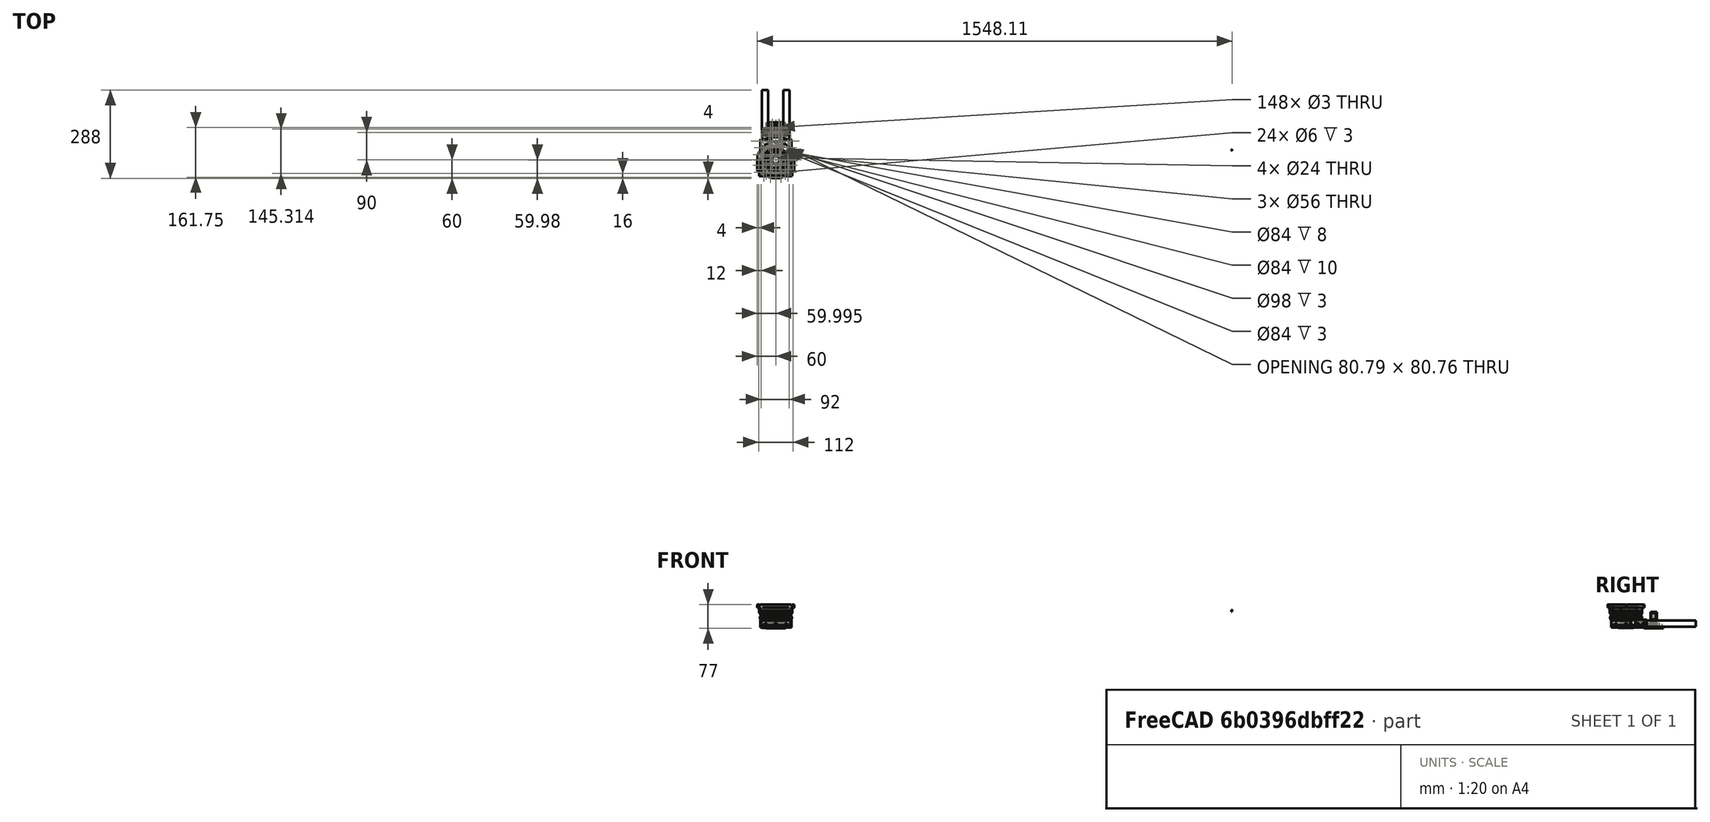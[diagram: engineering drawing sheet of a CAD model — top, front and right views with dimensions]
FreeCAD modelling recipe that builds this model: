
FCSTD DOCUMENT  (FreeCAD 0.19R24276 (Git))
Label: J-max_encoder_026
License: All rights reserved
LicenseURL: http://en.wikipedia.org/wiki/All_rights_reserved
objects: Part::Cylinder×255, Part::Compound×99, Part::Cut×96, Part::Box×95, Part::Chamfer×22, Part::FeaturePython×21, Part::MultiFuse×6, Part::Fillet×5, Mesh::Feature×5, Part::Mirroring×2
note: 601 computed .brp shape members not serialized (recipe doc carries the construction recipe); baked Part::Feature solids carry a one-line shape summary decoded from their .brp

FEATURE [Part::Cylinder] Cylinder120  label="Válec120"
  Angle = 360
  AttacherType = Attacher::AttachEngine3D
  Height = 10
  Radius = 52
FEATURE [Part::Cylinder] Cylinder121  label="Válec121"
  Angle = 360
  AttacherType = Attacher::AttachEngine3D
  Height = 10
  Radius = 60
FEATURE [Part::FeaturePython] wormgear026  # WARN: FeaturePython — macro-defined, semantics opaque (R4)
  AttacherType = Attacher::AttachEngine3D
  beta = 29.7292
  clearance = 0.25
  diameter = 78.8
  head = 0
  height = 20
  module = 1
  pressure_angle = 20
  reverse_pitch = true
  teeth = 45
  version = 0.0.3
FEATURE [Part::Cut] Cut057
  Base = -> Cylinder121
  Placement = pos=(0,0,10) rot=(0,0,1;0.034907rad)
  Tool = -> wormgear026
FEATURE [Part::FeaturePython] wormgear027  # WARN: FeaturePython — macro-defined, semantics opaque (R4)
  AttacherType = Attacher::AttachEngine3D
  Placement = pos=(0,0,0) rot=(0,0,1;0.009355rad)
  beta = 29.7292
  clearance = 0.25
  diameter = 78.8
  head = 0
  height = 20
  module = 1
  pressure_angle = 20
  reverse_pitch = false
  teeth = 45
  version = 0.0.3
FEATURE [Part::Cut] Cut056
  Base = -> Cylinder120
  Tool = -> wormgear027
FEATURE [Part::Compound] Compound157
  Links = -> [Cut057,Cut056]
FEATURE [Part::Cylinder] Cylinder132  label="Válec132"
  Angle = 360
  AttacherType = Attacher::AttachEngine3D
  Height = 40
  Placement = pos=(59,-17,0) rot=(0,0,1;0rad)
  Radius = 10
FEATURE [Part::Cylinder] Cylinder133  label="Válec133"
  Angle = 360
  AttacherType = Attacher::AttachEngine3D
  Height = 40
  Placement = pos=(-59,-17,0) rot=(0,0,1;0rad)
  Radius = 10
FEATURE [Part::Compound] Compound162
  Links = -> [Cylinder132,Cylinder133]
FEATURE [Part::Cylinder] Cylinder134  label="Válec134"
  Angle = 360
  AttacherType = Attacher::AttachEngine3D
  Height = 10
  Placement = pos=(0,0,20) rot=(0,0,1;0rad)
  Radius = 52
FEATURE [Part::Box] Box045  label="Krychle045"
  AttacherType = Attacher::AttachEngine3D
  Height = 10
  Length = 108
  Placement = pos=(-54,-53,20) rot=(0,0,1;0rad)
  Width = 36
FEATURE [Part::Cut] Cut062
  Base = -> Box045
  Placement = pos=(0,0,-20) rot=(0,0,1;0rad)
  Tool = -> Cylinder134
FEATURE [Part::Cut] Cut063
  Base = -> Cut062
  Tool = -> Compound162
FEATURE [Part::Cylinder] Cylinder135  label="Válec135"
  Angle = 360
  AttacherType = Attacher::AttachEngine3D
  Height = 10
  Placement = pos=(0,0,20) rot=(0,0,1;0rad)
  Radius = 52
FEATURE [Part::Box] Box046  label="Krychle046"
  AttacherType = Attacher::AttachEngine3D
  Height = 10
  Length = 108
  Placement = pos=(-54,-53,20) rot=(0,0,1;0rad)
  Width = 36
FEATURE [Part::Cut] Cut064
  Base = -> Box046
  Placement = pos=(0,0,-10) rot=(0,0,1;0rad)
  Tool = -> Cylinder135
FEATURE [Part::Cylinder] Cylinder136  label="Válec136"
  Angle = 360
  AttacherType = Attacher::AttachEngine3D
  Height = 20
  Placement = pos=(-24,-40,-5) rot=(1,0,0;1.5708rad)
  Radius = 1.5
FEATURE [Part::Cylinder] Cylinder137  label="Válec137"
  Angle = 360
  AttacherType = Attacher::AttachEngine3D
  Height = 20
  Placement = pos=(24,-40,-5) rot=(1,0,0;1.5708rad)
  Radius = 1.5
FEATURE [Part::Box] Box047  label="Krychle047"
  AttacherType = Attacher::AttachEngine3D
  Height = 6
  Length = 6
  Placement = pos=(-27,-47,-8) rot=(0,0,1;0rad)
  Width = 2
FEATURE [Part::Box] Box048  label="Krychle048"
  AttacherType = Attacher::AttachEngine3D
  Height = 6
  Length = 6
  Placement = pos=(21,-47,-8) rot=(0,0,1;0rad)
  Width = 2
FEATURE [Part::FeaturePython] Tube  # WARN: FeaturePython — macro-defined, semantics opaque (R4)
  AttacherType = Attacher::AttachEngine3D
  Height = 8
  InnerRadius = 42
  OuterRadius = 52
  Placement = pos=(0,0,-8) rot=(0,0,1;0rad)
FEATURE [Part::Box] Box049  label="Krychle049"
  AttacherType = Attacher::AttachEngine3D
  Height = 6
  Length = 6
  Placement = pos=(48,-45,4) rot=(0,0,1;0rad)
  Width = 2
FEATURE [Part::Cylinder] Cylinder138  label="Válec138"
  Angle = 360
  AttacherType = Attacher::AttachEngine3D
  Height = 40
  Placement = pos=(59,-17,0) rot=(0,0,1;0rad)
  Radius = 10
FEATURE [Part::Cylinder] Cylinder139  label="Válec139"
  Angle = 360
  AttacherType = Attacher::AttachEngine3D
  Height = 40
  Placement = pos=(-59,-17,0) rot=(0,0,1;0rad)
  Radius = 10
FEATURE [Part::Cylinder] Cylinder140  label="Válec140"
  Angle = 360
  AttacherType = Attacher::AttachEngine3D
  Height = 8
  Placement = pos=(0,0,20) rot=(0,0,1;0rad)
  Radius = 52
FEATURE [Part::Compound] Compound163
  Links = -> [Cylinder138,Cylinder139]
FEATURE [Part::Box] Box050  label="Krychle050"
  AttacherType = Attacher::AttachEngine3D
  Height = 8
  Length = 108
  Placement = pos=(-54,-53,20) rot=(0,0,1;0rad)
  Width = 36
FEATURE [Part::Cut] Cut065
  Base = -> Box050
  Placement = pos=(0,0,-20) rot=(0,0,1;0rad)
  Tool = -> Cylinder140
FEATURE [Part::Cut] Cut066
  Base = -> Cut065
  Placement = pos=(0,0,-8) rot=(0,0,1;0rad)
  Tool = -> Compound163
FEATURE [Part::Cylinder] Cylinder141  label="Válec141"
  Angle = 360
  AttacherType = Attacher::AttachEngine3D
  Height = 20
  Placement = pos=(51,-40,7) rot=(1,0,0;1.5708rad)
  Radius = 1.5
FEATURE [Part::Box] Box051  label="Krychle051"
  AttacherType = Attacher::AttachEngine3D
  Height = 6
  Length = 6
  Placement = pos=(-54,-45,4) rot=(0,0,1;0rad)
  Width = 2
FEATURE [Part::Compound] Compound169
  Links = -> [Box047,Box048,Box049,Box051]
FEATURE [Part::Cylinder] Cylinder142  label="Válec142"
  Angle = 360
  AttacherType = Attacher::AttachEngine3D
  Height = 20
  Placement = pos=(-51,-40,7) rot=(1,0,0;1.5708rad)
  Radius = 1.5
FEATURE [Part::Compound] Compound172
  Links = -> [Cylinder136,Cylinder137,Cylinder141,Cylinder142]
FEATURE [Part::Cylinder] Cylinder143  label="Válec143"
  Angle = 360
  AttacherType = Attacher::AttachEngine3D
  Height = 20
  Placement = pos=(0,-56,2) rot=(0,0,1;0rad)
  Radius = 1.5
FEATURE [Part::Cylinder] Cylinder144  label="Válec144"
  Angle = 360
  AttacherType = Attacher::AttachEngine3D
  Height = 20
  Placement = pos=(39.598,-39.598,2) rot=(0,0,1;0.785398rad)
  Radius = 1.5
FEATURE [Part::Cylinder] Cylinder145  label="Válec145"
  Angle = 360
  AttacherType = Attacher::AttachEngine3D
  Height = 20
  Placement = pos=(56,0,2) rot=(0,0,1;1.5708rad)
  Radius = 1.5
FEATURE [Part::Cylinder] Cylinder146  label="Válec146"
  Angle = 360
  AttacherType = Attacher::AttachEngine3D
  Height = 20
  Placement = pos=(39.598,39.598,2) rot=(0,0,1;2.35619rad)
  Radius = 1.5
FEATURE [Part::Cylinder] Cylinder147  label="Válec147"
  Angle = 360
  AttacherType = Attacher::AttachEngine3D
  Height = 20
  Placement = pos=(-1.2e-14,56,2) rot=(0,0,1;3.14159rad)
  Radius = 1.5
FEATURE [Part::Cylinder] Cylinder148  label="Válec148"
  Angle = 360
  AttacherType = Attacher::AttachEngine3D
  Height = 20
  Placement = pos=(-39.598,39.598,2) rot=(0,0,1;3.92699rad)
  Radius = 1.5
FEATURE [Part::Cylinder] Cylinder149  label="Válec149"
  Angle = 360
  AttacherType = Attacher::AttachEngine3D
  Height = 20
  Placement = pos=(-56,-1.3e-14,2) rot=(0,0,-1;1.5708rad)
  Radius = 1.5
FEATURE [Part::Cylinder] Cylinder150  label="Válec150"
  Angle = 360
  AttacherType = Attacher::AttachEngine3D
  Height = 20
  Placement = pos=(-39.598,-39.598,2) rot=(0,0,-1;0.785398rad)
  Radius = 1.5
FEATURE [Part::Compound] Compound164
  Links = -> [Cylinder143,Cylinder144,Cylinder145,Cylinder146,Cylinder147,Cylinder148,Cylinder149,Cylinder150]
FEATURE [Part::Cut] Cut067
  Base = -> Compound157
  Tool = -> Compound164
FEATURE [Part::Cylinder] Cylinder151  label="Válec151"
  Angle = 360
  AttacherType = Attacher::AttachEngine3D
  Height = 20
  Placement = pos=(-39.598,39.598,2) rot=(0,0,1;3.92699rad)
  Radius = 1.5
FEATURE [Part::Cylinder] Cylinder152  label="Válec152"
  Angle = 360
  AttacherType = Attacher::AttachEngine3D
  Height = 20
  Placement = pos=(-39.598,-39.598,2) rot=(0,0,-1;0.785398rad)
  Radius = 1.5
FEATURE [Part::Cylinder] Cylinder153  label="Válec153"
  Angle = 360
  AttacherType = Attacher::AttachEngine3D
  Height = 20
  Placement = pos=(56,0,2) rot=(0,0,1;1.5708rad)
  Radius = 1.5
FEATURE [Part::Cylinder] Cylinder154  label="Válec154"
  Angle = 360
  AttacherType = Attacher::AttachEngine3D
  Height = 20
  Placement = pos=(-1.2e-14,56,2) rot=(0,0,1;3.14159rad)
  Radius = 1.5
FEATURE [Part::Cylinder] Cylinder155  label="Válec155"
  Angle = 360
  AttacherType = Attacher::AttachEngine3D
  Height = 20
  Placement = pos=(0,-56,2) rot=(0,0,1;0rad)
  Radius = 1.5
FEATURE [Part::Cylinder] Cylinder156  label="Válec156"
  Angle = 360
  AttacherType = Attacher::AttachEngine3D
  Height = 20
  Placement = pos=(39.598,39.598,2) rot=(0,0,1;2.35619rad)
  Radius = 1.5
FEATURE [Part::Cylinder] Cylinder157  label="Válec157"
  Angle = 360
  AttacherType = Attacher::AttachEngine3D
  Height = 20
  Placement = pos=(-56,-1.3e-14,2) rot=(0,0,-1;1.5708rad)
  Radius = 1.5
FEATURE [Part::Cylinder] Cylinder158  label="Válec158"
  Angle = 360
  AttacherType = Attacher::AttachEngine3D
  Height = 20
  Placement = pos=(39.598,-39.598,2) rot=(0,0,1;0.785398rad)
  Radius = 1.5
FEATURE [Part::Compound] Compound165
  Links = -> [Cylinder155,Cylinder158,Cylinder153,Cylinder156,Cylinder154,Cylinder151,Cylinder157,Cylinder152]
FEATURE [Part::Cut] Cut068
  Base = -> Cut064
  Tool = -> Compound165
FEATURE [Part::Cylinder] Cylinder159  label="Válec159"
  Angle = 360
  AttacherType = Attacher::AttachEngine3D
  Height = 20
  Placement = pos=(-39.6,-39.6,-10) rot=(0,0,-1;0.785398rad)
  Radius = 4
FEATURE [Part::Cylinder] Cylinder160  label="Válec160"
  Angle = 360
  AttacherType = Attacher::AttachEngine3D
  Height = 20
  Placement = pos=(39.6,-39.6,-10) rot=(0,0,1;0.785398rad)
  Radius = 4
FEATURE [Part::Compound] Compound166
  Links = -> [Cylinder159,Cylinder160]
FEATURE [Part::Cylinder] Cylinder161  label="Válec161"
  Angle = 360
  AttacherType = Attacher::AttachEngine3D
  Height = 20
  Placement = pos=(39.6,-39.6,-10) rot=(0,0,1;0.785398rad)
  Radius = 4
FEATURE [Part::Cylinder] Cylinder162  label="Válec162"
  Angle = 360
  AttacherType = Attacher::AttachEngine3D
  Height = 20
  Placement = pos=(-39.6,-39.6,-10) rot=(0,0,-1;0.785398rad)
  Radius = 4
FEATURE [Part::Compound] Compound167
  Links = -> [Cylinder162,Cylinder161]
FEATURE [Part::Cut] Cut069
  Base = -> Cut067
  Tool = -> Compound166
FEATURE [Part::Cut] Cut070
  Base = -> Cut066
  Tool = -> Compound167
FEATURE [Part::Cut] Cut072
  Base = -> Cut070
  Tool = -> Compound169
FEATURE [Part::Cylinder] Cylinder163  label="Válec163"
  Angle = 360
  AttacherType = Attacher::AttachEngine3D
  Height = 20
  Placement = pos=(39.6,-39.6,-10) rot=(0,0,1;0.785398rad)
  Radius = 4
FEATURE [Part::Cylinder] Cylinder164  label="Válec164"
  Angle = 360
  AttacherType = Attacher::AttachEngine3D
  Height = 20
  Placement = pos=(-39.6,-39.6,-10) rot=(0,0,-1;0.785398rad)
  Radius = 4
FEATURE [Part::Compound] Compound168
  Links = -> [Cylinder164,Cylinder163]
FEATURE [Part::Cut] Cut071
  Base = -> Cut063
  Tool = -> Compound168
FEATURE [Part::Box] Box052  label="Krychle052"
  AttacherType = Attacher::AttachEngine3D
  Height = 6
  Length = 6
  Placement = pos=(48,-45,4) rot=(0,0,1;0rad)
  Width = 2
FEATURE [Part::Box] Box053  label="Krychle053"
  AttacherType = Attacher::AttachEngine3D
  Height = 6
  Length = 6
  Placement = pos=(17,-47,-8) rot=(0,0,1;0rad)
  Width = 2
FEATURE [Part::Box] Box054  label="Krychle054"
  AttacherType = Attacher::AttachEngine3D
  Height = 6
  Length = 6
  Placement = pos=(-23,-47,-8) rot=(0,0,1;0rad)
  Width = 2
FEATURE [Part::Box] Box055  label="Krychle055"
  AttacherType = Attacher::AttachEngine3D
  Height = 6
  Length = 6
  Placement = pos=(-54,-45,4) rot=(0,0,1;0rad)
  Width = 2
FEATURE [Part::Compound] Compound170
  Links = -> [Box054,Box053,Box052,Box055]
FEATURE [Part::Cut] Cut073
  Base = -> Cut071
  Tool = -> Compound170
FEATURE [Part::Box] Box056  label="Krychle056"
  AttacherType = Attacher::AttachEngine3D
  Height = 6
  Length = 6
  Placement = pos=(48,-45,4) rot=(0,0,1;0rad)
  Width = 2
FEATURE [Part::Box] Box057  label="Krychle057"
  AttacherType = Attacher::AttachEngine3D
  Height = 6
  Length = 6
  Placement = pos=(21,-47,-8) rot=(0,0,1;0rad)
  Width = 2
FEATURE [Part::Box] Box058  label="Krychle058"
  AttacherType = Attacher::AttachEngine3D
  Height = 6
  Length = 6
  Placement = pos=(-27,-47,-8) rot=(0,0,1;0rad)
  Width = 2
FEATURE [Part::Box] Box059  label="Krychle059"
  AttacherType = Attacher::AttachEngine3D
  Height = 6
  Length = 6
  Placement = pos=(-54,-45,4) rot=(0,0,1;0rad)
  Width = 2
FEATURE [Part::Compound] Compound171
  Links = -> [Box058,Box057,Box056,Box059]
FEATURE [Part::Cylinder] Cylinder165  label="Válec165"
  Angle = 360
  AttacherType = Attacher::AttachEngine3D
  Height = 20
  Placement = pos=(-24,-40,-5) rot=(1,0,0;1.5708rad)
  Radius = 1.5
FEATURE [Part::Cylinder] Cylinder166  label="Válec166"
  Angle = 360
  AttacherType = Attacher::AttachEngine3D
  Height = 20
  Placement = pos=(24,-40,-5) rot=(1,0,0;1.5708rad)
  Radius = 1.5
FEATURE [Part::Cut] Cut074
  Base = -> Tube
  Tool = -> Compound171
FEATURE [Part::Cut] Cut075
  Base = -> Cut074
  Tool = -> Compound172
FEATURE [Part::Cylinder] Cylinder167  label="Válec167"
  Angle = 360
  AttacherType = Attacher::AttachEngine3D
  Height = 20
  Placement = pos=(51,-40,7) rot=(1,0,0;1.5708rad)
  Radius = 1.5
FEATURE [Part::Cylinder] Cylinder168  label="Válec168"
  Angle = 360
  AttacherType = Attacher::AttachEngine3D
  Height = 20
  Placement = pos=(-51,-40,7) rot=(1,0,0;1.5708rad)
  Radius = 1.5
FEATURE [Part::Compound] Compound173
  Links = -> [Cylinder165,Cylinder166,Cylinder167,Cylinder168]
FEATURE [Part::Cut] Cut076
  Base = -> Cut072
  Tool = -> Compound173
FEATURE [Part::Cylinder] Cylinder169  label="Válec169"
  Angle = 360
  AttacherType = Attacher::AttachEngine3D
  Height = 20
  Placement = pos=(-20,-40,-5) rot=(1,0,0;1.5708rad)
  Radius = 1.5
FEATURE [Part::Cylinder] Cylinder170  label="Válec170"
  Angle = 360
  AttacherType = Attacher::AttachEngine3D
  Height = 20
  Placement = pos=(20,-40,-5) rot=(1,0,0;1.5708rad)
  Radius = 1.5
FEATURE [Part::Cylinder] Cylinder171  label="Válec171"
  Angle = 360
  AttacherType = Attacher::AttachEngine3D
  Height = 20
  Placement = pos=(51,-40,7) rot=(1,0,0;1.5708rad)
  Radius = 1.5
FEATURE [Part::Cylinder] Cylinder172  label="Válec172"
  Angle = 360
  AttacherType = Attacher::AttachEngine3D
  Height = 20
  Placement = pos=(-51,-40,7) rot=(1,0,0;1.5708rad)
  Radius = 1.5
FEATURE [Part::Compound] Compound174
  Links = -> [Cylinder169,Cylinder170,Cylinder171,Cylinder172]
FEATURE [Part::Cut] Cut077
  Base = -> Cut073
  Tool = -> Compound174
FEATURE [Part::Box] Box060  label="Krychle060"
  AttacherType = Attacher::AttachEngine3D
  Height = 2
  Length = 6
  Placement = pos=(-3,41,-4) rot=(0,0,1;0rad)
  Width = 8
FEATURE [Part::Cylinder] Cylinder173  label="Válec173"
  Angle = 360
  AttacherType = Attacher::AttachEngine3D
  Height = 20
  Placement = pos=(0,45,-18) rot=(0,0,1;0rad)
  Radius = 1.5
FEATURE [Part::Box] Box061  label="Krychle061"
  AttacherType = Attacher::AttachEngine3D
  Height = 2
  Length = 6
  Placement = pos=(-31.1127,26.8701,-4) rot=(0,0,1;0.785398rad)
  Width = 8
FEATURE [Part::Box] Box062  label="Krychle062"
  AttacherType = Attacher::AttachEngine3D
  Height = 2
  Length = 6
  Placement = pos=(-41,-3,-4) rot=(0,0,1;1.5708rad)
  Width = 8
FEATURE [Part::Box] Box063  label="Krychle063"
  AttacherType = Attacher::AttachEngine3D
  Height = 2
  Length = 6
  Placement = pos=(-26.8701,-31.1127,-4) rot=(0,0,1;2.35619rad)
  Width = 8
FEATURE [Part::Box] Box064  label="Krychle064"
  AttacherType = Attacher::AttachEngine3D
  Height = 2
  Length = 6
  Placement = pos=(3,-41,-4) rot=(0,0,1;3.14159rad)
  Width = 8
FEATURE [Part::Box] Box065  label="Krychle065"
  AttacherType = Attacher::AttachEngine3D
  Height = 2
  Length = 6
  Placement = pos=(31.1127,-26.8701,-4) rot=(0,0,1;3.92699rad)
  Width = 8
FEATURE [Part::Box] Box066  label="Krychle066"
  AttacherType = Attacher::AttachEngine3D
  Height = 2
  Length = 6
  Placement = pos=(41,3,-4) rot=(0,0,-1;1.5708rad)
  Width = 8
FEATURE [Part::Box] Box067  label="Krychle067"
  AttacherType = Attacher::AttachEngine3D
  Height = 2
  Length = 6
  Placement = pos=(26.8701,31.1127,-4) rot=(0,0,-1;0.785398rad)
  Width = 8
FEATURE [Part::Cylinder] Cylinder174  label="Válec174"
  Angle = 360
  AttacherType = Attacher::AttachEngine3D
  Height = 20
  Placement = pos=(-31.8198,31.8198,-18) rot=(0,0,1;0.785398rad)
  Radius = 1.5
FEATURE [Part::Cylinder] Cylinder175  label="Válec175"
  Angle = 360
  AttacherType = Attacher::AttachEngine3D
  Height = 20
  Placement = pos=(-45,-6e-15,-18) rot=(0,0,1;1.5708rad)
  Radius = 1.5
FEATURE [Part::Cylinder] Cylinder176  label="Válec176"
  Angle = 360
  AttacherType = Attacher::AttachEngine3D
  Height = 20
  Placement = pos=(-31.8198,-31.8198,-18) rot=(0,0,1;2.35619rad)
  Radius = 1.5
FEATURE [Part::Cylinder] Cylinder177  label="Válec177"
  Angle = 360
  AttacherType = Attacher::AttachEngine3D
  Height = 20
  Placement = pos=(1.4e-14,-45,-18) rot=(0,0,1;3.14159rad)
  Radius = 1.5
FEATURE [Part::Cylinder] Cylinder178  label="Válec178"
  Angle = 360
  AttacherType = Attacher::AttachEngine3D
  Height = 20
  Placement = pos=(31.8198,-31.8198,-18) rot=(0,0,1;3.92699rad)
  Radius = 1.5
FEATURE [Part::Compound] Compound175
  Links = -> [Box060,Box061,Box062,Box063,Box064,Box065,Box066,Box067]
  Placement = pos=(0,0,0) rot=(0,0,1;0.392699rad)
FEATURE [Part::Cut] Cut078
  Base = -> Cut075
  Tool = -> Compound175
FEATURE [Part::Cylinder] Cylinder179  label="Válec179"
  Angle = 360
  AttacherType = Attacher::AttachEngine3D
  Height = 20
  Placement = pos=(45,1.9e-14,-18) rot=(0,0,-1;1.5708rad)
  Radius = 1.5
FEATURE [Part::Cylinder] Cylinder180  label="Válec180"
  Angle = 360
  AttacherType = Attacher::AttachEngine3D
  Height = 20
  Placement = pos=(31.8198,31.8198,-18) rot=(0,0,-1;0.785398rad)
  Radius = 1.5
FEATURE [Part::Compound] Compound176
  Links = -> [Cylinder173,Cylinder174,Cylinder175,Cylinder176,Cylinder177,Cylinder178,Cylinder179,Cylinder180]
  Placement = pos=(0,0,0) rot=(0,0,1;0.392699rad)
FEATURE [Part::Cut] Cut079
  Base = -> Cut078
  Tool = -> Compound176
FEATURE [Part::Compound] Compound177  label="joint_max_monoblok1"
  Links = -> [Cut077,Cut079,Cut076,Cut069,Cut068]
FEATURE [Part::Fillet] Fillet
  Base = -> Compound177
  Edges = 2 edges r=9: [Edge42,Edge278]
FEATURE [Part::Fillet] Fillet001  label="J-max_monoblok2"
  Base = -> Fillet
  Edges = 2 edges r=8: [Edge30,Edge90]
FEATURE [Part::Box] Box108  label="Krychle108"
  AttacherType = Attacher::AttachEngine3D
  Height = 10
  Length = 10
  Placement = pos=(50,-43,10) rot=(0,0,1;0rad)
  Width = 43
FEATURE [Part::Cylinder] Cylinder300  label="Válec300"
  Angle = 360
  AttacherType = Attacher::AttachEngine3D
  Height = 10
  Placement = pos=(60,-43,10) rot=(0,0,1;0rad)
  Radius = 6
FEATURE [Part::Box] Box109  label="Krychle109"
  AttacherType = Attacher::AttachEngine3D
  Height = 10
  Length = 10
  Placement = pos=(-60,-43,10) rot=(0,0,1;0rad)
  Width = 43
FEATURE [Part::Cylinder] Cylinder301  label="Válec301"
  Angle = 360
  AttacherType = Attacher::AttachEngine3D
  Height = 10
  Placement = pos=(-60,-43,10) rot=(0,0,1;0rad)
  Radius = 6
FEATURE [Part::Cylinder] Cylinder302  label="Válec302"
  Angle = 360
  AttacherType = Attacher::AttachEngine3D
  Height = 20
  Placement = pos=(39.598,-39.598,2) rot=(0,0,1;0.785398rad)
  Radius = 1.5
FEATURE [Part::Cylinder] Cylinder303  label="Válec303"
  Angle = 360
  AttacherType = Attacher::AttachEngine3D
  Height = 20
  Placement = pos=(39.598,39.598,2) rot=(0,0,1;2.35619rad)
  Radius = 1.5
FEATURE [Part::Compound] Compound239
  Links = -> [Box109,Box108]
FEATURE [Part::Compound] Compound241
  Links = -> [Cylinder300,Cylinder301]
FEATURE [Part::Cylinder] Cylinder304  label="Válec304"
  Angle = 360
  AttacherType = Attacher::AttachEngine3D
  Height = 20
  Placement = pos=(-39.598,39.598,2) rot=(0,0,1;3.92699rad)
  Radius = 1.5
FEATURE [Part::Cylinder] Cylinder305  label="Válec305"
  Angle = 360
  AttacherType = Attacher::AttachEngine3D
  Height = 20
  Placement = pos=(-39.598,-39.598,2) rot=(0,0,-1;0.785398rad)
  Radius = 1.5
FEATURE [Part::Cylinder] Cylinder306  label="Válec306"
  Angle = 360
  AttacherType = Attacher::AttachEngine3D
  Height = 20
  Placement = pos=(56,0,2) rot=(0,0,1;1.5708rad)
  Radius = 1.5
FEATURE [Part::Cylinder] Cylinder307  label="Válec307"
  Angle = 360
  AttacherType = Attacher::AttachEngine3D
  Height = 20
  Placement = pos=(-1.2e-14,56,2) rot=(0,0,1;3.14159rad)
  Radius = 1.5
FEATURE [Part::Cylinder] Cylinder308  label="Válec308"
  Angle = 360
  AttacherType = Attacher::AttachEngine3D
  Height = 20
  Placement = pos=(-56,-1.3e-14,2) rot=(0,0,-1;1.5708rad)
  Radius = 1.5
FEATURE [Part::Cylinder] Cylinder309  label="Válec309"
  Angle = 360
  AttacherType = Attacher::AttachEngine3D
  Height = 20
  Placement = pos=(0,-56,2) rot=(0,0,1;0rad)
  Radius = 1.5
FEATURE [Part::Compound] Compound240
  Links = -> [Cylinder309,Cylinder302,Cylinder306,Cylinder303,Cylinder307,Cylinder304,Cylinder308,Cylinder305]
FEATURE [Part::Cut] Cut129
  Base = -> Compound239
  Tool = -> Compound240
FEATURE [Part::Cut] Cut130
  Base = -> Cut129
  Tool = -> Compound241
FEATURE [Part::Fillet] Fillet002
  Base = -> Cut130
  Edges = 2 edges r=4: [Edge4,Edge43]
FEATURE [Part::Compound] Compound242  label="J-max_monoblok"
  Links = -> [Fillet002,Fillet001]
FEATURE [Part::Cylinder] Cylinder623  label="Válec623"
  Angle = 360
  AttacherType = Attacher::AttachEngine3D
  Height = 20
  Placement = pos=(-31.8198,31.8198,-18) rot=(0,0,1;0.785398rad)
  Radius = 1.5
FEATURE [Part::Cylinder] Cylinder625  label="Válec625"
  Angle = 360
  AttacherType = Attacher::AttachEngine3D
  Height = 16
  Placement = pos=(2e-15,16,2) rot=(0,0,-1;1.1781rad)
  Radius = 1.5
FEATURE [Part::Cylinder] Cylinder626  label="Válec626"
  Angle = 360
  AttacherType = Attacher::AttachEngine3D
  Height = 16
  Placement = pos=(-16,7e-15,2) rot=(0,0,1;0.392699rad)
  Radius = 1.5
FEATURE [Part::Cylinder] Cylinder627  label="Válec627"
  Angle = 360
  AttacherType = Attacher::AttachEngine3D
  Height = 16
  Placement = pos=(-1.2e-14,-16,2) rot=(0,0,1;1.96349rad)
  Radius = 1.5
FEATURE [Part::Cylinder] Cylinder628  label="Válec628"
  Angle = 360
  AttacherType = Attacher::AttachEngine3D
  Height = 20
  Placement = pos=(0,45,-18) rot=(0,0,1;0rad)
  Radius = 1.5
FEATURE [Part::Cylinder] Cylinder629  label="Válec629"
  Angle = 360
  AttacherType = Attacher::AttachEngine3D
  Height = 20
  Placement = pos=(-31.8198,-31.8198,-18) rot=(0,0,1;2.35619rad)
  Radius = 1.5
FEATURE [Part::Cylinder] Cylinder630  label="Válec630"
  Angle = 360
  AttacherType = Attacher::AttachEngine3D
  Height = 16
  Placement = pos=(16,0,2) rot=(0,0,1;3.53429rad)
  Radius = 1.5
FEATURE [Part::Compound] Compound653
  Links = -> [Cylinder630,Cylinder625,Cylinder626,Cylinder627]
  Placement = pos=(0,0,-111) rot=(0,0,1;0rad)
FEATURE [Part::Cylinder] Cylinder631  label="Válec631"
  Angle = 360
  AttacherType = Attacher::AttachEngine3D
  Height = 20
  Placement = pos=(45,1.9e-14,-18) rot=(0,0,-1;1.5708rad)
  Radius = 1.5
FEATURE [Part::Cylinder] Cylinder632  label="Válec632"
  Angle = 360
  AttacherType = Attacher::AttachEngine3D
  Height = 20
  Placement = pos=(-45,-6e-15,-18) rot=(0,0,1;1.5708rad)
  Radius = 1.5
FEATURE [Part::Cylinder] Cylinder633  label="Válec633"
  Angle = 360
  AttacherType = Attacher::AttachEngine3D
  Height = 20
  Placement = pos=(31.8198,31.8198,-18) rot=(0,0,-1;0.785398rad)
  Radius = 1.5
FEATURE [Part::Cylinder] Cylinder638  label="Válec638"
  Angle = 360
  AttacherType = Attacher::AttachEngine3D
  Height = 20
  Placement = pos=(31.8198,-31.8198,-18) rot=(0,0,1;3.92699rad)
  Radius = 1.5
FEATURE [Part::Cylinder] Cylinder639  label="Válec639"
  Angle = 360
  AttacherType = Attacher::AttachEngine3D
  Height = 20
  Placement = pos=(1.4e-14,-45,-18) rot=(0,0,1;3.14159rad)
  Radius = 1.5
FEATURE [Part::Compound] Compound654
  Links = -> [Cylinder628,Cylinder623,Cylinder632,Cylinder629,Cylinder639,Cylinder638,Cylinder631,Cylinder633]
  Placement = pos=(0,0,-87) rot=(0,0,1;0.392699rad)
FEATURE [Part::FeaturePython] Tube038  # WARN: FeaturePython — macro-defined, semantics opaque (R4)
  AttacherType = Attacher::AttachEngine3D
  Height = 2
  InnerRadius = 12
  OuterRadius = 52
  Placement = pos=(0,0,-100) rot=(0,0,1;0rad)
FEATURE [Part::FeaturePython] Tube040  # WARN: FeaturePython — macro-defined, semantics opaque (R4)
  AttacherType = Attacher::AttachEngine3D
  Height = 3
  InnerRadius = 42
  OuterRadius = 52
  Placement = pos=(0,0,-11) rot=(0,0,1;0rad)
FEATURE [Part::Cut] Cut285
  Base = -> Tube038
  Tool = -> Compound653
FEATURE [Part::Cut] Cut287
  Base = -> Cut285
  Tool = -> Compound654
FEATURE [Part::Cylinder] Cylinder652  label="Válec652"
  Angle = 360
  AttacherType = Attacher::AttachEngine3D
  Height = 20
  Placement = pos=(-31.8198,-31.8198,-18) rot=(0,0,1;2.35619rad)
  Radius = 1.5
FEATURE [Part::Cylinder] Cylinder653  label="Válec653"
  Angle = 360
  AttacherType = Attacher::AttachEngine3D
  Height = 20
  Placement = pos=(0,45,-18) rot=(0,0,1;0rad)
  Radius = 1.5
FEATURE [Part::Cylinder] Cylinder654  label="Válec654"
  Angle = 360
  AttacherType = Attacher::AttachEngine3D
  Height = 20
  Placement = pos=(45,1.9e-14,-18) rot=(0,0,-1;1.5708rad)
  Radius = 1.5
FEATURE [Part::Cylinder] Cylinder655  label="Válec655"
  Angle = 360
  AttacherType = Attacher::AttachEngine3D
  Height = 20
  Placement = pos=(1.4e-14,-45,-18) rot=(0,0,1;3.14159rad)
  Radius = 1.5
FEATURE [Part::Cylinder] Cylinder656  label="Válec656"
  Angle = 360
  AttacherType = Attacher::AttachEngine3D
  Height = 20
  Placement = pos=(31.8198,31.8198,-18) rot=(0,0,-1;0.785398rad)
  Radius = 1.5
FEATURE [Part::Cylinder] Cylinder657  label="Válec657"
  Angle = 360
  AttacherType = Attacher::AttachEngine3D
  Height = 20
  Placement = pos=(31.8198,-31.8198,-18) rot=(0,0,1;3.92699rad)
  Radius = 1.5
FEATURE [Part::Cylinder] Cylinder658  label="Válec658"
  Angle = 360
  AttacherType = Attacher::AttachEngine3D
  Height = 20
  Placement = pos=(-31.8198,31.8198,-18) rot=(0,0,1;0.785398rad)
  Radius = 1.5
FEATURE [Part::Cylinder] Cylinder659  label="Válec659"
  Angle = 360
  AttacherType = Attacher::AttachEngine3D
  Height = 20
  Placement = pos=(-45,-6e-15,-18) rot=(0,0,1;1.5708rad)
  Radius = 1.5
FEATURE [Part::Compound] Compound660
  Links = -> [Cylinder653,Cylinder658,Cylinder659,Cylinder652,Cylinder655,Cylinder657,Cylinder654,Cylinder656]
  Placement = pos=(0,0,0) rot=(0,0,1;0.392699rad)
FEATURE [Part::Cut] Cut290  label="J-max_motor-high-washer_A1"
  Base = -> Tube040
  Placement = pos=(0,0,-4) rot=(0,0,1;0rad)
  Tool = -> Compound660
FEATURE [Part::Chamfer] Chamfer018  label="J-max_motor-high-washer_A"
  Base = -> Cut290
  Edges = 1 edges r=1: [Edge3]
  Placement = pos=(0,0,4) rot=(0,0,1;0rad)
FEATURE [Part::Cylinder] Cylinder660  label="Válec660"
  Angle = 360
  AttacherType = Attacher::AttachEngine3D
  Height = 20
  Placement = pos=(0,45,-18) rot=(0,0,1;0rad)
  Radius = 1.5
FEATURE [Part::Cylinder] Cylinder661  label="Válec661"
  Angle = 360
  AttacherType = Attacher::AttachEngine3D
  Height = 20
  Placement = pos=(-31.8198,-31.8198,-18) rot=(0,0,1;2.35619rad)
  Radius = 1.5
FEATURE [Part::Cylinder] Cylinder662  label="Válec662"
  Angle = 360
  AttacherType = Attacher::AttachEngine3D
  Height = 20
  Placement = pos=(-31.8198,31.8198,-18) rot=(0,0,1;0.785398rad)
  Radius = 1.5
FEATURE [Part::Cylinder] Cylinder663  label="Válec663"
  Angle = 360
  AttacherType = Attacher::AttachEngine3D
  Height = 20
  Placement = pos=(1.4e-14,-45,-18) rot=(0,0,1;3.14159rad)
  Radius = 1.5
FEATURE [Part::Cylinder] Cylinder664  label="Válec664"
  Angle = 360
  AttacherType = Attacher::AttachEngine3D
  Height = 20
  Placement = pos=(-45,-6e-15,-18) rot=(0,0,1;1.5708rad)
  Radius = 1.5
FEATURE [Part::Cylinder] Cylinder665  label="Válec665"
  Angle = 360
  AttacherType = Attacher::AttachEngine3D
  Height = 20
  Placement = pos=(45,1.9e-14,-18) rot=(0,0,-1;1.5708rad)
  Radius = 1.5
FEATURE [Part::Cylinder] Cylinder666  label="Válec666"
  Angle = 360
  AttacherType = Attacher::AttachEngine3D
  Height = 20
  Placement = pos=(31.8198,31.8198,-18) rot=(0,0,-1;0.785398rad)
  Radius = 1.5
FEATURE [Part::Cylinder] Cylinder667  label="Válec667"
  Angle = 360
  AttacherType = Attacher::AttachEngine3D
  Height = 20
  Placement = pos=(31.8198,-31.8198,-18) rot=(0,0,1;3.92699rad)
  Radius = 1.5
FEATURE [Part::Compound] Compound661
  Links = -> [Cylinder660,Cylinder662,Cylinder664,Cylinder661,Cylinder663,Cylinder667,Cylinder665,Cylinder666]
  Placement = pos=(0,0,-8) rot=(0,0,1;0.392699rad)
FEATURE [Part::FeaturePython] Tube041  # WARN: FeaturePython — macro-defined, semantics opaque (R4)
  AttacherType = Attacher::AttachEngine3D
  Height = 10
  InnerRadius = 42
  OuterRadius = 49
  Placement = pos=(0,0,-22) rot=(0,0,1;0rad)
FEATURE [Part::Cut] Cut291
  Base = -> Tube041
  Placement = pos=(0,0,-10) rot=(0,0,1;0rad)
  Tool = -> Compound661
FEATURE [Part::FeaturePython] Tube042  # WARN: FeaturePython — macro-defined, semantics opaque (R4)
  AttacherType = Attacher::AttachEngine3D
  Height = 3
  InnerRadius = 49
  OuterRadius = 52
  Placement = pos=(0,0,-22) rot=(0,0,1;0rad)
FEATURE [Part::Chamfer] Chamfer017
  Base = -> Tube042
  Edges = 1 edges r=1: [Edge1]
  Placement = pos=(0,0,-10) rot=(0,0,1;0rad)
FEATURE [Part::Compound] Compound662  label="J-max_motor-high-washer_B"
  Links = -> [Cut291,Chamfer017]
  Placement = pos=(0,0,11) rot=(0,0,1;0rad)
FEATURE [Part::FeaturePython] Tube060  # WARN: FeaturePython — macro-defined, semantics opaque (R4)
  AttacherType = Attacher::AttachEngine3D
  Height = 9
  InnerRadius = 31
  OuterRadius = 36
  Placement = pos=(0,0,-99) rot=(0,0,1;0rad)
FEATURE [Part::Chamfer] Chamfer019
  Base = -> Tube060
  Edges = 1 edges r=1: [Edge4]
FEATURE [Part::FeaturePython] Tube061  # WARN: FeaturePython — macro-defined, semantics opaque (R4)
  AttacherType = Attacher::AttachEngine3D
  Height = 1
  InnerRadius = 26
  OuterRadius = 36
  Placement = pos=(0,0,-98) rot=(0,0,1;0rad)
FEATURE [Part::Compound] Compound663  label="J-max_undermotor-undercover"
  Links = -> [Chamfer019,Tube061,Cut287]
  Placement = pos=(0,0,77) rot=(0,0,1;0rad)
FEATURE [Part::Box] Box104  label="Krychle104"
  AttacherType = Attacher::AttachEngine3D
  Height = 2
  Length = 10
  Placement = pos=(11,-3,6) rot=(0,0,1;0rad)
  Width = 6
FEATURE [Part::Box] Box105  label="Krychle105"
  AttacherType = Attacher::AttachEngine3D
  Height = 2
  Length = 10
  Placement = pos=(-11,3,6) rot=(0,0,1;3.14159rad)
  Width = 6
FEATURE [Part::Box] Box106  label="Krychle106"
  AttacherType = Attacher::AttachEngine3D
  Height = 2
  Length = 10
  Placement = pos=(3,11,6) rot=(0,0,1;1.5708rad)
  Width = 6
FEATURE [Part::Box] Box107  label="Krychle107"
  AttacherType = Attacher::AttachEngine3D
  Height = 2
  Length = 10
  Placement = pos=(-3,-11,6) rot=(0,0,-1;1.5708rad)
  Width = 6
FEATURE [Part::Cylinder] Cylinder272  label="Válec272"
  Angle = 360
  AttacherType = Attacher::AttachEngine3D
  Height = 16
  Placement = pos=(16,0,2) rot=(0,0,1;3.53429rad)
  Radius = 1.5
FEATURE [Part::Compound] Compound232
  Links = -> [Box104,Box106,Box105,Box107]
  Placement = pos=(0,0,-111) rot=(0,0,1;0rad)
FEATURE [Part::FeaturePython] Tube029  # WARN: FeaturePython — macro-defined, semantics opaque (R4)
  AttacherType = Attacher::AttachEngine3D
  Height = 5
  InnerRadius = 12
  OuterRadius = 52
  Placement = pos=(0,0,-100) rot=(0,0,1;0rad)
FEATURE [Part::FeaturePython] Tube030  # WARN: FeaturePython — macro-defined, semantics opaque (R4)
  AttacherType = Attacher::AttachEngine3D
  Height = 4
  InnerRadius = 12
  OuterRadius = 24.8
  Placement = pos=(0,0,-103) rot=(0,0,1;0rad)
FEATURE [Part::FeaturePython] Tube031  # WARN: FeaturePython — macro-defined, semantics opaque (R4)
  AttacherType = Attacher::AttachEngine3D
  Height = 11
  InnerRadius = 12
  OuterRadius = 20
  Placement = pos=(0,0,-111) rot=(0,0,1;0rad)
FEATURE [Part::Cylinder] Cylinder273  label="Válec273"
  Angle = 360
  AttacherType = Attacher::AttachEngine3D
  Height = 16
  Placement = pos=(-16,7e-15,2) rot=(0,0,1;0.392699rad)
  Radius = 1.5
FEATURE [Part::Cylinder] Cylinder274  label="Válec274"
  Angle = 360
  AttacherType = Attacher::AttachEngine3D
  Height = 16
  Placement = pos=(-1.2e-14,-16,2) rot=(0,0,1;1.96349rad)
  Radius = 1.5
FEATURE [Part::Cylinder] Cylinder275  label="Válec275"
  Angle = 360
  AttacherType = Attacher::AttachEngine3D
  Height = 16
  Placement = pos=(2e-15,16,2) rot=(0,0,-1;1.1781rad)
  Radius = 1.5
FEATURE [Part::Compound] Compound233
  Links = -> [Cylinder272,Cylinder275,Cylinder273,Cylinder274]
  Placement = pos=(0,0,-117) rot=(0,0,1;0rad)
FEATURE [Part::Cut] Cut124
  Base = -> Tube030
  Placement = pos=(0,0,-1) rot=(0,0,1;0rad)
  Tool = -> Compound233
FEATURE [Part::Cylinder] Cylinder276  label="Válec276"
  Angle = 360
  AttacherType = Attacher::AttachEngine3D
  Height = 16
  Placement = pos=(16,0,2) rot=(0,0,1;3.53429rad)
  Radius = 1.5
FEATURE [Part::Cylinder] Cylinder277  label="Válec277"
  Angle = 360
  AttacherType = Attacher::AttachEngine3D
  Height = 16
  Placement = pos=(-16,7e-15,2) rot=(0,0,1;0.392699rad)
  Radius = 1.5
FEATURE [Part::Cylinder] Cylinder278  label="Válec278"
  Angle = 360
  AttacherType = Attacher::AttachEngine3D
  Height = 16
  Placement = pos=(-1.2e-14,-16,2) rot=(0,0,1;1.96349rad)
  Radius = 1.5
FEATURE [Part::Cylinder] Cylinder279  label="Válec279"
  Angle = 360
  AttacherType = Attacher::AttachEngine3D
  Height = 16
  Placement = pos=(2e-15,16,2) rot=(0,0,-1;1.1781rad)
  Radius = 1.5
FEATURE [Part::Compound] Compound234
  Links = -> [Cylinder276,Cylinder279,Cylinder277,Cylinder278]
  Placement = pos=(0,0,-117) rot=(0,0,1;0rad)
FEATURE [Part::Cut] Cut123
  Base = -> Tube031
  Tool = -> Compound234
FEATURE [Part::Cut] Cut126
  Base = -> Cut123
  Tool = -> Compound232
FEATURE [Part::Cylinder] Cylinder280  label="Válec280"
  Angle = 360
  AttacherType = Attacher::AttachEngine3D
  Height = 16
  Placement = pos=(2e-15,16,2) rot=(0,0,-1;1.1781rad)
  Radius = 1.5
FEATURE [Part::Cylinder] Cylinder281  label="Válec281"
  Angle = 360
  AttacherType = Attacher::AttachEngine3D
  Height = 16
  Placement = pos=(16,0,2) rot=(0,0,1;3.53429rad)
  Radius = 1.5
FEATURE [Part::Cylinder] Cylinder282  label="Válec282"
  Angle = 360
  AttacherType = Attacher::AttachEngine3D
  Height = 16
  Placement = pos=(-16,7e-15,2) rot=(0,0,1;0.392699rad)
  Radius = 1.5
FEATURE [Part::Cylinder] Cylinder283  label="Válec283"
  Angle = 360
  AttacherType = Attacher::AttachEngine3D
  Height = 16
  Placement = pos=(-1.2e-14,-16,2) rot=(0,0,1;1.96349rad)
  Radius = 1.5
FEATURE [Part::Cylinder] Cylinder284  label="Válec284"
  Angle = 360
  AttacherType = Attacher::AttachEngine3D
  Height = 20
  Placement = pos=(-45,-6e-15,-18) rot=(0,0,1;1.5708rad)
  Radius = 1.5
FEATURE [Part::Cylinder] Cylinder285  label="Válec285"
  Angle = 360
  AttacherType = Attacher::AttachEngine3D
  Height = 20
  Placement = pos=(-31.8198,-31.8198,-18) rot=(0,0,1;2.35619rad)
  Radius = 1.5
FEATURE [Part::Cylinder] Cylinder286  label="Válec286"
  Angle = 360
  AttacherType = Attacher::AttachEngine3D
  Height = 20
  Placement = pos=(0,45,-18) rot=(0,0,1;0rad)
  Radius = 1.5
FEATURE [Part::Cylinder] Cylinder287  label="Válec287"
  Angle = 360
  AttacherType = Attacher::AttachEngine3D
  Height = 20
  Placement = pos=(45,1.9e-14,-18) rot=(0,0,-1;1.5708rad)
  Radius = 1.5
FEATURE [Part::Cylinder] Cylinder288  label="Válec288"
  Angle = 360
  AttacherType = Attacher::AttachEngine3D
  Height = 20
  Placement = pos=(-31.8198,31.8198,-18) rot=(0,0,1;0.785398rad)
  Radius = 1.5
FEATURE [Part::Cylinder] Cylinder289  label="Válec289"
  Angle = 360
  AttacherType = Attacher::AttachEngine3D
  Height = 20
  Placement = pos=(31.8198,-31.8198,-18) rot=(0,0,1;3.92699rad)
  Radius = 1.5
FEATURE [Part::Cylinder] Cylinder290  label="Válec290"
  Angle = 360
  AttacherType = Attacher::AttachEngine3D
  Height = 20
  Placement = pos=(31.8198,31.8198,-18) rot=(0,0,-1;0.785398rad)
  Radius = 1.5
FEATURE [Part::Cylinder] Cylinder291  label="Válec291"
  Angle = 360
  AttacherType = Attacher::AttachEngine3D
  Height = 20
  Placement = pos=(1.4e-14,-45,-18) rot=(0,0,1;3.14159rad)
  Radius = 1.5
FEATURE [Part::Cylinder] Cylinder292  label="Válec292"
  Angle = 360
  AttacherType = Attacher::AttachEngine3D
  Height = 3
  Placement = pos=(31.8198,-31.8198,-18) rot=(0,0,1;3.92699rad)
  Radius = 3
FEATURE [Part::Cylinder] Cylinder293  label="Válec293"
  Angle = 360
  AttacherType = Attacher::AttachEngine3D
  Height = 3
  Placement = pos=(-31.8198,-31.8198,-18) rot=(0,0,1;2.35619rad)
  Radius = 3
FEATURE [Part::Cylinder] Cylinder294  label="Válec294"
  Angle = 360
  AttacherType = Attacher::AttachEngine3D
  Height = 3
  Placement = pos=(0,45,-18) rot=(0,0,1;0rad)
  Radius = 3
FEATURE [Part::Cylinder] Cylinder295  label="Válec295"
  Angle = 360
  AttacherType = Attacher::AttachEngine3D
  Height = 3
  Placement = pos=(45,1.9e-14,-18) rot=(0,0,-1;1.5708rad)
  Radius = 3
FEATURE [Part::Cylinder] Cylinder296  label="Válec296"
  Angle = 360
  AttacherType = Attacher::AttachEngine3D
  Height = 3
  Placement = pos=(-45,-6e-15,-18) rot=(0,0,1;1.5708rad)
  Radius = 3
FEATURE [Part::Cylinder] Cylinder297  label="Válec297"
  Angle = 360
  AttacherType = Attacher::AttachEngine3D
  Height = 3
  Placement = pos=(-31.8198,31.8198,-18) rot=(0,0,1;0.785398rad)
  Radius = 3
FEATURE [Part::Cylinder] Cylinder298  label="Válec298"
  Angle = 360
  AttacherType = Attacher::AttachEngine3D
  Height = 3
  Placement = pos=(1.4e-14,-45,-18) rot=(0,0,1;3.14159rad)
  Radius = 3
FEATURE [Part::Cylinder] Cylinder299  label="Válec299"
  Angle = 360
  AttacherType = Attacher::AttachEngine3D
  Height = 3
  Placement = pos=(31.8198,31.8198,-18) rot=(0,0,-1;0.785398rad)
  Radius = 3
FEATURE [Part::Compound] Compound235
  Links = -> [Cylinder281,Cylinder280,Cylinder282,Cylinder283]
  Placement = pos=(0,0,-117) rot=(0,0,1;0rad)
FEATURE [Part::Cut] Cut125
  Base = -> Tube029
  Tool = -> Compound235
FEATURE [Part::Compound] Compound236
  Links = -> [Cylinder286,Cylinder288,Cylinder284,Cylinder285,Cylinder291,Cylinder289,Cylinder287,Cylinder290]
  Placement = pos=(0,0,-87) rot=(0,0,1;0.392699rad)
FEATURE [Part::Cut] Cut127
  Base = -> Cut125
  Tool = -> Compound236
FEATURE [Part::Compound] Compound237
  Links = -> [Cylinder294,Cylinder297,Cylinder296,Cylinder293,Cylinder298,Cylinder292,Cylinder295,Cylinder299]
  Placement = pos=(0,0,-82) rot=(0,0,1;0.392699rad)
FEATURE [Part::Cut] Cut128
  Base = -> Cut127
  Tool = -> Compound237
FEATURE [Part::Chamfer] Chamfer003
  Base = -> Cut128
  Edges = 1 edges r=1: [Edge3]
FEATURE [Part::Chamfer] Chamfer004
  Base = -> Cut126
  Edges = 1 edges r=1: [Edge6]
  Placement = pos=(0,0,-1) rot=(0,0,1;0rad)
FEATURE [Part::Compound] Compound238  label="J-max_undermotor-cover"
  Links = -> [Cut124,Chamfer003,Chamfer004]
  Placement = pos=(0,0,72) rot=(0,0,1;0rad)
FEATURE [Part::Cylinder] Cylinder073  label="Válec073"
  Angle = 360
  AttacherType = Attacher::AttachEngine3D
  Height = 4
  Placement = pos=(1500,0,-4) rot=(0,0,1;0rad)
  Radius = 1.5
FEATURE [Part::Compound] Compound116
  Links = -> [Cylinder073]
  Placement = pos=(2060.63,-1353.48,-2) rot=(0.55557,0.83147,0;3.14159rad)
FEATURE [Part::FeaturePython] Tube036  # WARN: FeaturePython — macro-defined, semantics opaque (R4)
  AttacherType = Attacher::AttachEngine3D
  Height = 15
  InnerRadius = 12
  OuterRadius = 20.1
  Placement = pos=(0,0,17) rot=(0,0,1;0rad)
FEATURE [Part::FeaturePython] Tube037  # WARN: FeaturePython — macro-defined, semantics opaque (R4)
  AttacherType = Attacher::AttachEngine3D
  Height = 9
  InnerRadius = 19.5
  OuterRadius = 24.8
  Placement = pos=(0,0,23) rot=(0,0,1;0rad)
FEATURE [Part::Cylinder] Cylinder600  label="Válec600"
  Angle = 360
  AttacherType = Attacher::AttachEngine3D
  Height = 30
  Placement = pos=(-1.2e-14,-16,2) rot=(0,0,1;1.96349rad)
  Radius = 1.5
FEATURE [Part::Cylinder] Cylinder601  label="Válec601"
  Angle = 360
  AttacherType = Attacher::AttachEngine3D
  Height = 3
  Placement = pos=(-1.2e-14,-16,2) rot=(0,0,1;1.96349rad)
  Radius = 3
FEATURE [Part::Cylinder] Cylinder602  label="Válec602"
  Angle = 360
  AttacherType = Attacher::AttachEngine3D
  Height = 3
  Placement = pos=(2e-15,16,2) rot=(0,0,-1;1.1781rad)
  Radius = 3
FEATURE [Part::Cylinder] Cylinder603  label="Válec603"
  Angle = 360
  AttacherType = Attacher::AttachEngine3D
  Height = 3
  Placement = pos=(-16,7e-15,2) rot=(0,0,1;0.392699rad)
  Radius = 3
FEATURE [Part::Cylinder] Cylinder604  label="Válec604"
  Angle = 360
  AttacherType = Attacher::AttachEngine3D
  Height = 30
  Placement = pos=(16,0,2) rot=(0,0,1;3.53429rad)
  Radius = 1.5
FEATURE [Part::Cylinder] Cylinder605  label="Válec605"
  Angle = 360
  AttacherType = Attacher::AttachEngine3D
  Height = 30
  Placement = pos=(2e-15,16,2) rot=(0,0,-1;1.1781rad)
  Radius = 1.5
FEATURE [Part::Cylinder] Cylinder606  label="Válec606"
  Angle = 360
  AttacherType = Attacher::AttachEngine3D
  Height = 30
  Placement = pos=(-16,7e-15,2) rot=(0,0,1;0.392699rad)
  Radius = 1.5
FEATURE [Part::Compound] Compound647
  Links = -> [Cylinder600,Cylinder606,Cylinder605,Cylinder604]
  Placement = pos=(0,0,-2) rot=(0,0,1;0rad)
FEATURE [Part::Cylinder] Cylinder607  label="Válec607"
  Angle = 360
  AttacherType = Attacher::AttachEngine3D
  Height = 3
  Placement = pos=(16,0,2) rot=(0,0,1;3.53429rad)
  Radius = 3
FEATURE [Part::Compound] Compound646
  Links = -> [Cylinder601,Cylinder603,Cylinder602,Cylinder607]
  Placement = pos=(0,0,27) rot=(0,0,1;0rad)
FEATURE [Part::Cut] Cut276
  Base = -> Tube036
  Tool = -> Compound646
FEATURE [Part::Cut] Cut278
  Base = -> Cut276
  Tool = -> Compound647
FEATURE [Part::Box] Box290  label="Krychle290"
  AttacherType = Attacher::AttachEngine3D
  Height = 2
  Length = 10
  Placement = pos=(-11,3,6) rot=(0,0,1;3.14159rad)
  Width = 6
FEATURE [Part::Cylinder] Cylinder608  label="Válec608"
  Angle = 360
  AttacherType = Attacher::AttachEngine3D
  Height = 30
  Placement = pos=(-1.2e-14,-16,2) rot=(0,0,1;1.96349rad)
  Radius = 1.5
FEATURE [Part::Cylinder] Cylinder609  label="Válec609"
  Angle = 360
  AttacherType = Attacher::AttachEngine3D
  Height = 30
  Placement = pos=(16,0,2) rot=(0,0,1;3.53429rad)
  Radius = 1.5
FEATURE [Part::Cylinder] Cylinder610  label="Válec610"
  Angle = 360
  AttacherType = Attacher::AttachEngine3D
  Height = 30
  Placement = pos=(-16,7e-15,2) rot=(0,0,1;0.392699rad)
  Radius = 1.5
FEATURE [Part::Cylinder] Cylinder611  label="Válec611"
  Angle = 360
  AttacherType = Attacher::AttachEngine3D
  Height = 30
  Placement = pos=(2e-15,16,2) rot=(0,0,-1;1.1781rad)
  Radius = 1.5
FEATURE [Part::Compound] Compound648
  Links = -> [Cylinder608,Cylinder610,Cylinder611,Cylinder609]
  Placement = pos=(0,0,5) rot=(0,0,1;0.785398rad)
FEATURE [Part::Box] Box291  label="Krychle291"
  AttacherType = Attacher::AttachEngine3D
  Height = 2
  Length = 10
  Placement = pos=(11,-3,6) rot=(0,0,1;0rad)
  Width = 6
FEATURE [Part::Box] Box292  label="Krychle292"
  AttacherType = Attacher::AttachEngine3D
  Height = 2
  Length = 10
  Placement = pos=(-3,-11,6) rot=(0,0,-1;1.5708rad)
  Width = 6
FEATURE [Part::Box] Box293  label="Krychle293"
  AttacherType = Attacher::AttachEngine3D
  Height = 2
  Length = 10
  Placement = pos=(3,11,6) rot=(0,0,1;1.5708rad)
  Width = 6
FEATURE [Part::Compound] Compound650
  Links = -> [Box291,Box293,Box290,Box292]
  Placement = pos=(0,0,15) rot=(0,0,1;0.785398rad)
FEATURE [Part::Cut] Cut279
  Base = -> Cut278
  Tool = -> Compound650
FEATURE [Part::Cut] Cut277
  Base = -> Cut279
  Tool = -> Compound648
FEATURE [Part::Compound] Compound649
  Links = -> [Tube037,Cut277]
FEATURE [Part::Chamfer] Chamfer016  label="J-max_arm-bearing-fix"
  Base = -> Compound649
  Edges = 1 edges r=1: [Edge8]
  Placement = pos=(0,0,-24) rot=(1,0,0;3.14159rad)
FEATURE [Part::Box] Box294  label="Krychle294"
  AttacherType = Attacher::AttachEngine3D
  Height = 18
  Length = 32
  Placement = pos=(19,30,5) rot=(0,0,1;0rad)
  Width = 38
FEATURE [Part::Box] Box295  label="Krychle295"
  AttacherType = Attacher::AttachEngine3D
  Height = 20
  Length = 20
  Placement = pos=(-45,28,8) rot=(0,0,1;0rad)
  Width = 200
FEATURE [Part::Cylinder] Cylinder668  label="Válec668"
  Angle = 360
  AttacherType = Attacher::AttachEngine3D
  Height = 20
  Placement = pos=(11,54.5,3) rot=(0,0,1;0rad)
  Radius = 8
FEATURE [Part::Box] Box296  label="Krychle296"
  AttacherType = Attacher::AttachEngine3D
  Height = 18
  Length = 35
  Placement = pos=(10,36,5) rot=(0,0,1;0rad)
  Width = 17
FEATURE [Part::Box] Box297  label="Krychle297"
  AttacherType = Attacher::AttachEngine3D
  Height = 18
  Length = 11
  Placement = pos=(37,0,5) rot=(0,0,1;0rad)
  Width = 38
FEATURE [Part::Box] Box298  label="Krychle298"
  AttacherType = Attacher::AttachEngine3D
  Height = 20
  Length = 20
  Placement = pos=(25,28,8) rot=(0,0,1;0rad)
  Width = 200
FEATURE [Part::Compound] Compound210
  Links = -> [Box298,Box295]
FEATURE [Part::Box] Box299  label="Krychle299"
  AttacherType = Attacher::AttachEngine3D
  Height = 18
  Length = 32
  Placement = pos=(19,30,5) rot=(0,0,1;0rad)
  Width = 38
FEATURE [Part::Cylinder] Cylinder669  label="Válec669"
  Angle = 360
  AttacherType = Attacher::AttachEngine3D
  Height = 20
  Placement = pos=(11,54.5,3) rot=(0,0,1;0rad)
  Radius = 8
FEATURE [Part::Box] Box300  label="Krychle300"
  AttacherType = Attacher::AttachEngine3D
  Height = 18
  Length = 35
  Placement = pos=(10,36,5) rot=(0,0,1;0rad)
  Width = 17
FEATURE [Part::Box] Box301  label="Krychle301"
  AttacherType = Attacher::AttachEngine3D
  Height = 18
  Length = 11
  Placement = pos=(37,0,5) rot=(0,0,1;0rad)
  Width = 36
FEATURE [Part::Cylinder] Cylinder670  label="Válec670"
  Angle = 360
  AttacherType = Attacher::AttachEngine3D
  Height = 150
  Placement = pos=(-57,56,18) rot=(0,1,0;1.5708rad)
  Radius = 2.5
FEATURE [Part::FeaturePython] Tube012  # WARN: FeaturePython — macro-defined, semantics opaque (R4)
  AttacherType = Attacher::AttachEngine3D
  Height = 3
  InnerRadius = 28
  OuterRadius = 48
  Placement = pos=(0,0,5) rot=(0,0,1;0rad)
FEATURE [Part::FeaturePython] Tube013  # WARN: FeaturePython — macro-defined, semantics opaque (R4)
  AttacherType = Attacher::AttachEngine3D
  Height = 15
  InnerRadius = 34
  OuterRadius = 48
  Placement = pos=(0,0,8) rot=(0,0,1;0rad)
FEATURE [Part::Cut] Cut292
  Base = -> Box296
  Tool = -> Cylinder668
FEATURE [Part::MultiFuse] Fusion
  Shapes = -> [Box294,Box297,Cut292]
FEATURE [Part::Mirroring] mirror  label="Fusion (mirrored)"
  Base = (0,0,0)
  Normal = (1,0,0)
  Source = -> Fusion
FEATURE [Part::Cut] Cut293
  Base = -> Box300
  Tool = -> Cylinder669
FEATURE [Part::MultiFuse] Fusion001
  Shapes = -> [Box299,Box301,Cut293]
FEATURE [Part::MultiFuse] Fusion002
  Shapes = -> [Tube013,mirror,Fusion001]
FEATURE [Part::Cut] Cut294
  Base = -> Fusion002
  Tool = -> Compound210
FEATURE [Part::Cylinder] Cylinder671  label="Válec671"
  Angle = 360
  AttacherType = Attacher::AttachEngine3D
  Height = 30
  Placement = pos=(-57,38,18) rot=(0,1,0;1.5708rad)
  Radius = 2.5
FEATURE [Part::Cylinder] Cylinder672  label="Válec672"
  Angle = 360
  AttacherType = Attacher::AttachEngine3D
  Height = 30
  Placement = pos=(28,38,18) rot=(0,1,0;1.5708rad)
  Radius = 2.5
FEATURE [Part::Compound] Compound211
  Links = -> [Cylinder670,Cylinder671,Cylinder672]
FEATURE [Part::Cut] Cut295
  Base = -> Cut294
  Tool = -> Compound211
FEATURE [Part::Cylinder] Cylinder673  label="Válec673"
  Angle = 360
  AttacherType = Attacher::AttachEngine3D
  Height = 30
  Placement = pos=(0,44,10) rot=(0,0,-1;1.1781rad)
  Radius = 1.5
FEATURE [Part::Box] Box302  label="Krychle302"
  AttacherType = Attacher::AttachEngine3D
  Height = 2
  Length = 6
  Placement = pos=(-3,41,16) rot=(0,0,1;0rad)
  Width = 8
FEATURE [Part::Box] Box303  label="Krychle303"
  AttacherType = Attacher::AttachEngine3D
  Height = 2
  Length = 6
  Placement = pos=(-41,-3,16) rot=(0,0,1;1.5708rad)
  Width = 8
FEATURE [Part::Box] Box304  label="Krychle304"
  AttacherType = Attacher::AttachEngine3D
  Height = 2
  Length = 6
  Placement = pos=(3,-41,16) rot=(0,0,1;3.14159rad)
  Width = 8
FEATURE [Part::Box] Box305  label="Krychle305"
  AttacherType = Attacher::AttachEngine3D
  Height = 2
  Length = 6
  Placement = pos=(41,3,16) rot=(0,0,-1;1.5708rad)
  Width = 8
FEATURE [Part::Compound] Compound212
  Links = -> [Box302,Box303,Box304,Box305]
FEATURE [Part::Cut] Cut296
  Base = -> Cut295
  Tool = -> Compound212
FEATURE [Part::Cylinder] Cylinder674  label="Válec674"
  Angle = 360
  AttacherType = Attacher::AttachEngine3D
  Height = 30
  Placement = pos=(-44,0,10) rot=(0,0,1;0.392699rad)
  Radius = 1.5
FEATURE [Part::Cylinder] Cylinder675  label="Válec675"
  Angle = 360
  AttacherType = Attacher::AttachEngine3D
  Height = 30
  Placement = pos=(1.5e-14,-44,10) rot=(0,0,1;1.96349rad)
  Radius = 1.5
FEATURE [Part::Cylinder] Cylinder676  label="Válec676"
  Angle = 360
  AttacherType = Attacher::AttachEngine3D
  Height = 30
  Placement = pos=(44,3.4e-14,10) rot=(0,0,1;3.53429rad)
  Radius = 1.5
FEATURE [Part::Compound] Compound213
  Links = -> [Cylinder673,Cylinder674,Cylinder675,Cylinder676]
FEATURE [Part::Cut] Cut297
  Base = -> Cut296
  Tool = -> Compound213
FEATURE [Part::Box] Box  label="Krychle"
  AttacherType = Attacher::AttachEngine3D
  Height = 2
  Length = 6
  Placement = pos=(-51,58,12) rot=(0,0,1;0rad)
  Width = 6
FEATURE [Part::Cylinder] Cylinder  label="Válec"
  Angle = 360
  AttacherType = Attacher::AttachEngine3D
  Height = 30
  Placement = pos=(-48,61,0) rot=(0,0,1;0rad)
  Radius = 1.5
FEATURE [Part::Box] Box306  label="Krychle306"
  AttacherType = Attacher::AttachEngine3D
  Height = 2
  Length = 6
  Placement = pos=(-25,58,12) rot=(0,0,1;0rad)
  Width = 6
FEATURE [Part::Cylinder] Cylinder677  label="Válec677"
  Angle = 360
  AttacherType = Attacher::AttachEngine3D
  Height = 30
  Placement = pos=(-22,61,0) rot=(0,0,1;0rad)
  Radius = 1.5
FEATURE [Part::Box] Box307  label="Krychle307"
  AttacherType = Attacher::AttachEngine3D
  Height = 2
  Length = 6
  Placement = pos=(45,58,12) rot=(0,0,1;0rad)
  Width = 6
FEATURE [Part::Box] Box308  label="Krychle308"
  AttacherType = Attacher::AttachEngine3D
  Height = 2
  Length = 6
  Placement = pos=(19,58,12) rot=(0,0,1;0rad)
  Width = 6
FEATURE [Part::Box] Box309  label="Krychle309"
  AttacherType = Attacher::AttachEngine3D
  Height = 18
  Length = 3
  Placement = pos=(48,14,5) rot=(0,0,1;0rad)
  Width = 16
FEATURE [Part::Box] Box310  label="Krychle310"
  AttacherType = Attacher::AttachEngine3D
  Height = 18
  Length = 3
  Placement = pos=(-51,14,5) rot=(0,0,1;0rad)
  Width = 16
FEATURE [Part::Cylinder] Cylinder678  label="Válec678"
  Angle = 360
  AttacherType = Attacher::AttachEngine3D
  Height = 30
  Placement = pos=(48,61,0) rot=(0,0,1;0rad)
  Radius = 1.5
FEATURE [Part::Cylinder] Cylinder679  label="Válec679"
  Angle = 360
  AttacherType = Attacher::AttachEngine3D
  Height = 30
  Placement = pos=(22,61,0) rot=(0,0,1;0rad)
  Radius = 1.5
FEATURE [Part::Compound] Compound
  Links = -> [Cylinder,Cylinder677,Cylinder678,Cylinder679]
  Placement = pos=(0,0,7) rot=(0,0,1;0rad)
FEATURE [Part::Compound] Compound664
  Links = -> [Box,Box306,Box307,Box308]
FEATURE [Part::Cut] Cut
  Base = -> Cut297
  Tool = -> Compound664
FEATURE [Part::Cut] Cut298
  Base = -> Cut
  Tool = -> Compound
FEATURE [Part::Chamfer] Chamfer
  Base = -> Box310
  Edges = 1 edges r=2.9: [Edge1]
FEATURE [Part::Chamfer] Chamfer033
  Base = -> Box309
  Edges = 1 edges r=2.9: [Edge5]
FEATURE [Part::Cylinder] Cylinder680  label="Válec680"
  Angle = 360
  AttacherType = Attacher::AttachEngine3D
  Height = 10
  Placement = pos=(-19,56,18) rot=(0,1,0;1.5708rad)
  Radius = 8
FEATURE [Part::Cylinder] Cylinder681  label="Válec681"
  Angle = 360
  AttacherType = Attacher::AttachEngine3D
  Height = 10
  Placement = pos=(9,56,18) rot=(0,1,0;1.5708rad)
  Radius = 8
FEATURE [Part::Compound] Compound665
  Links = -> [Cylinder680,Cylinder681]
FEATURE [Part::Box] Box311  label="Krychle311"
  AttacherType = Attacher::AttachEngine3D
  Height = 2
  Length = 6
  Placement = pos=(-26.8701,-31.1127,16) rot=(0,0,1;2.35619rad)
  Width = 8
FEATURE [Part::Cylinder] Cylinder682  label="Válec682"
  Angle = 360
  AttacherType = Attacher::AttachEngine3D
  Height = 30
  Placement = pos=(-31.1127,-31.1127,10) rot=(0,0,1;1.1781rad)
  Radius = 1.5
FEATURE [Part::Box] Box312  label="Krychle312"
  AttacherType = Attacher::AttachEngine3D
  Height = 2
  Length = 6
  Placement = pos=(31.1127,-26.8701,16) rot=(0,0,1;3.92699rad)
  Width = 8
FEATURE [Part::Compound] Compound652
  Links = -> [Box311,Box312]
FEATURE [Part::Cylinder] Cylinder683  label="Válec683"
  Angle = 360
  AttacherType = Attacher::AttachEngine3D
  Height = 30
  Placement = pos=(31.1127,-31.1127,10) rot=(0,0,1;2.74889rad)
  Radius = 1.5
FEATURE [Part::Compound] Compound667
  Links = -> [Cylinder682,Cylinder683]
FEATURE [Part::Cut] Cut299
  Base = -> Cut298
  Tool = -> Compound665
FEATURE [Part::Chamfer] Chamfer034
  Base = -> Cut299
  Edges = 2 edges r=2: [Edge163,Edge202]
FEATURE [Part::Fillet] Fillet003
  Base = -> Chamfer034
  Edges = 2 edges r=3: [Edge4,Edge291]
FEATURE [Part::Compound] Compound666
  Links = -> [Chamfer,Chamfer033,Fillet003]
FEATURE [Part::Compound] Compound651
  Links = -> [Tube012,Compound666]
FEATURE [Part::Cut] Cut300
  Base = -> Compound651
  Tool = -> Compound652
FEATURE [Part::Cut] Cut301  label="J-max_bear-rotator1"
  Base = -> Cut300
  Tool = -> Compound667
FEATURE [Part::FeaturePython] Tube062  # WARN: FeaturePython — macro-defined, semantics opaque (R4)
  AttacherType = Attacher::AttachEngine3D
  Height = 3
  InnerRadius = 28
  OuterRadius = 48
  Placement = pos=(0,0,5) rot=(0,0,1;0rad)
FEATURE [Part::Compound] Compound668  label="J-max_bear-rotator"
  Links = -> [Tube062,Cut301]
  Placement = pos=(0,0,-24) rot=(0,1,0;3.14159rad)
FEATURE [Part::FeaturePython] Tube035  # WARN: FeaturePython — macro-defined, semantics opaque (R4)
  AttacherType = Attacher::AttachEngine3D
  Height = 8
  InnerRadius = 28
  OuterRadius = 34
  Placement = pos=(0,0,23) rot=(0,0,1;0rad)
FEATURE [Part::Box] Box313  label="Krychle313"
  AttacherType = Attacher::AttachEngine3D
  Height = 20
  Length = 20
  Placement = pos=(-45,28,8) rot=(0,0,1;0rad)
  Width = 200
FEATURE [Part::FeaturePython] Tube063  # WARN: FeaturePython — macro-defined, semantics opaque (R4)
  AttacherType = Attacher::AttachEngine3D
  Height = 8
  InnerRadius = 34
  OuterRadius = 48
  Placement = pos=(0,0,23) rot=(0,0,1;0rad)
FEATURE [Part::Box] Box314  label="Krychle314"
  AttacherType = Attacher::AttachEngine3D
  Height = 8
  Length = 32
  Placement = pos=(19,30,5) rot=(0,0,1;0rad)
  Width = 38
FEATURE [Part::Cylinder] Cylinder612  label="Válec612"
  Angle = 360
  AttacherType = Attacher::AttachEngine3D
  Height = 20
  Placement = pos=(11,54.5,3) rot=(0,0,1;0rad)
  Radius = 8
FEATURE [Part::Box] Box315  label="Krychle315"
  AttacherType = Attacher::AttachEngine3D
  Height = 8
  Length = 35
  Placement = pos=(10,36,5) rot=(0,0,1;0rad)
  Width = 17
FEATURE [Part::Cut] Cut280
  Base = -> Box315
  Tool = -> Cylinder612
FEATURE [Part::Box] Box316  label="Krychle316"
  AttacherType = Attacher::AttachEngine3D
  Height = 8
  Length = 11
  Placement = pos=(37,0,5) rot=(0,0,1;0rad)
  Width = 38
FEATURE [Part::MultiFuse] Fusion015
  Placement = pos=(0,0,18) rot=(0,0,1;0rad)
  Shapes = -> [Box314,Box316,Cut280]
FEATURE [Part::Mirroring] mirror005  label="Fusion (mirrored)005"
  Base = (0,0,0)
  Normal = (1,0,0)
  Source = -> Fusion015
FEATURE [Part::Box] Box317  label="Krychle317"
  AttacherType = Attacher::AttachEngine3D
  Height = 20
  Length = 20
  Placement = pos=(25,28,8) rot=(0,0,1;0rad)
  Width = 200
FEATURE [Part::Compound] Compound655
  Links = -> [Box317,Box313]
FEATURE [Part::Box] Box318  label="Krychle318"
  AttacherType = Attacher::AttachEngine3D
  Height = 8
  Length = 32
  Placement = pos=(19,30,5) rot=(0,0,1;0rad)
  Width = 38
FEATURE [Part::Cylinder] Cylinder613  label="Válec613"
  Angle = 360
  AttacherType = Attacher::AttachEngine3D
  Height = 20
  Placement = pos=(11,54.5,3) rot=(0,0,1;0rad)
  Radius = 8
FEATURE [Part::Box] Box319  label="Krychle319"
  AttacherType = Attacher::AttachEngine3D
  Height = 8
  Length = 35
  Placement = pos=(10,36,5) rot=(0,0,1;0rad)
  Width = 17
FEATURE [Part::Cut] Cut281
  Base = -> Box319
  Tool = -> Cylinder613
FEATURE [Part::Box] Box320  label="Krychle320"
  AttacherType = Attacher::AttachEngine3D
  Height = 8
  Length = 11
  Placement = pos=(37,0,5) rot=(0,0,1;0rad)
  Width = 36
FEATURE [Part::MultiFuse] Fusion016
  Placement = pos=(0,0,18) rot=(0,0,1;0rad)
  Shapes = -> [Box318,Box320,Cut281]
FEATURE [Part::MultiFuse] Fusion017
  Shapes = -> [Tube063,mirror005,Fusion016]
FEATURE [Part::Cut] Cut282
  Base = -> Fusion017
  Tool = -> Compound655
FEATURE [Part::Cylinder] Cylinder614  label="Válec614"
  Angle = 360
  AttacherType = Attacher::AttachEngine3D
  Height = 150
  Placement = pos=(-57,56,18) rot=(0,1,0;1.5708rad)
  Radius = 2.5
FEATURE [Part::Cylinder] Cylinder615  label="Válec615"
  Angle = 360
  AttacherType = Attacher::AttachEngine3D
  Height = 30
  Placement = pos=(-57,38,18) rot=(0,1,0;1.5708rad)
  Radius = 2.5
FEATURE [Part::Cylinder] Cylinder616  label="Válec616"
  Angle = 360
  AttacherType = Attacher::AttachEngine3D
  Height = 30
  Placement = pos=(28,38,18) rot=(0,1,0;1.5708rad)
  Radius = 2.5
FEATURE [Part::Compound] Compound656
  Links = -> [Cylinder614,Cylinder615,Cylinder616]
FEATURE [Part::Cut] Cut283
  Base = -> Cut282
  Tool = -> Compound656
FEATURE [Part::Cylinder] Cylinder617  label="Válec617"
  Angle = 360
  AttacherType = Attacher::AttachEngine3D
  Height = 30
  Placement = pos=(0,44,10) rot=(0,0,-1;1.1781rad)
  Radius = 1.5
FEATURE [Part::Box] Box321  label="Krychle321"
  AttacherType = Attacher::AttachEngine3D
  Height = 2
  Length = 6
  Placement = pos=(-3,41,16) rot=(0,0,1;0rad)
  Width = 8
FEATURE [Part::Box] Box322  label="Krychle322"
  AttacherType = Attacher::AttachEngine3D
  Height = 2
  Length = 6
  Placement = pos=(-41,-3,16) rot=(0,0,1;1.5708rad)
  Width = 8
FEATURE [Part::Box] Box323  label="Krychle323"
  AttacherType = Attacher::AttachEngine3D
  Height = 2
  Length = 6
  Placement = pos=(3,-41,16) rot=(0,0,1;3.14159rad)
  Width = 8
FEATURE [Part::Box] Box324  label="Krychle324"
  AttacherType = Attacher::AttachEngine3D
  Height = 2
  Length = 6
  Placement = pos=(41,3,16) rot=(0,0,-1;1.5708rad)
  Width = 8
FEATURE [Part::Compound] Compound657
  Links = -> [Box321,Box322,Box323,Box324]
FEATURE [Part::Cut] Cut284
  Base = -> Cut283
  Tool = -> Compound657
FEATURE [Part::Cylinder] Cylinder618  label="Válec618"
  Angle = 360
  AttacherType = Attacher::AttachEngine3D
  Height = 30
  Placement = pos=(-44,0,10) rot=(0,0,1;0.392699rad)
  Radius = 1.5
FEATURE [Part::Cylinder] Cylinder619  label="Válec619"
  Angle = 360
  AttacherType = Attacher::AttachEngine3D
  Height = 30
  Placement = pos=(1.5e-14,-44,10) rot=(0,0,1;1.96349rad)
  Radius = 1.5
FEATURE [Part::Cylinder] Cylinder620  label="Válec620"
  Angle = 360
  AttacherType = Attacher::AttachEngine3D
  Height = 30
  Placement = pos=(44,3.4e-14,10) rot=(0,0,1;3.53429rad)
  Radius = 1.5
FEATURE [Part::Compound] Compound658
  Links = -> [Cylinder617,Cylinder618,Cylinder619,Cylinder620]
FEATURE [Part::Cut] Cut302
  Base = -> Cut284
  Tool = -> Compound658
FEATURE [Part::Box] Box325  label="Krychle325"
  AttacherType = Attacher::AttachEngine3D
  Height = 2
  Length = 6
  Placement = pos=(-51,58,12) rot=(0,0,1;0rad)
  Width = 6
FEATURE [Part::Cylinder] Cylinder621  label="Válec621"
  Angle = 360
  AttacherType = Attacher::AttachEngine3D
  Height = 30
  Placement = pos=(-48,61,0) rot=(0,0,1;0rad)
  Radius = 1.5
FEATURE [Part::Box] Box326  label="Krychle326"
  AttacherType = Attacher::AttachEngine3D
  Height = 2
  Length = 6
  Placement = pos=(-25,58,12) rot=(0,0,1;0rad)
  Width = 6
FEATURE [Part::Cylinder] Cylinder622  label="Válec622"
  Angle = 360
  AttacherType = Attacher::AttachEngine3D
  Height = 30
  Placement = pos=(-22,61,0) rot=(0,0,1;0rad)
  Radius = 1.5
FEATURE [Part::Box] Box327  label="Krychle327"
  AttacherType = Attacher::AttachEngine3D
  Height = 2
  Length = 6
  Placement = pos=(45,58,12) rot=(0,0,1;0rad)
  Width = 6
FEATURE [Part::Box] Box328  label="Krychle328"
  AttacherType = Attacher::AttachEngine3D
  Height = 2
  Length = 6
  Placement = pos=(19,58,12) rot=(0,0,1;0rad)
  Width = 6
FEATURE [Part::Compound] Compound669
  Links = -> [Box325,Box326,Box327,Box328]
FEATURE [Part::Cut] Cut286
  Base = -> Cut302
  Tool = -> Compound669
FEATURE [Part::Cylinder] Cylinder684  label="Válec684"
  Angle = 360
  AttacherType = Attacher::AttachEngine3D
  Height = 30
  Placement = pos=(48,61,0) rot=(0,0,1;0rad)
  Radius = 1.5
FEATURE [Part::Cylinder] Cylinder624  label="Válec624"
  Angle = 360
  AttacherType = Attacher::AttachEngine3D
  Height = 30
  Placement = pos=(22,61,0) rot=(0,0,1;0rad)
  Radius = 1.5
FEATURE [Part::Compound] Compound659
  Links = -> [Cylinder621,Cylinder622,Cylinder684,Cylinder624]
  Placement = pos=(0,0,7) rot=(0,0,1;0rad)
FEATURE [Part::Cut] Cut303
  Base = -> Cut286
  Tool = -> Compound659
FEATURE [Part::Cylinder] Cylinder685  label="Válec685"
  Angle = 360
  AttacherType = Attacher::AttachEngine3D
  Height = 10
  Placement = pos=(-19,56,18) rot=(0,1,0;1.5708rad)
  Radius = 8
FEATURE [Part::Cylinder] Cylinder686  label="Válec686"
  Angle = 360
  AttacherType = Attacher::AttachEngine3D
  Height = 10
  Placement = pos=(9,56,18) rot=(0,1,0;1.5708rad)
  Radius = 8
FEATURE [Part::Compound] Compound670
  Links = -> [Cylinder685,Cylinder686]
FEATURE [Part::Cut] Cut288
  Base = -> Cut303
  Tool = -> Compound670
FEATURE [Part::Cylinder] Cylinder687  label="Válec687"
  Angle = 360
  AttacherType = Attacher::AttachEngine3D
  Height = 3
  Placement = pos=(0,44,10) rot=(0,0,-1;1.1781rad)
  Radius = 3
FEATURE [Part::Cylinder] Cylinder634  label="Válec634"
  Angle = 360
  AttacherType = Attacher::AttachEngine3D
  Height = 3
  Placement = pos=(-44,0,10) rot=(0,0,1;0.392699rad)
  Radius = 3
FEATURE [Part::Cylinder] Cylinder635  label="Válec635"
  Angle = 360
  AttacherType = Attacher::AttachEngine3D
  Height = 3
  Placement = pos=(1.5e-14,-44,10) rot=(0,0,1;1.96349rad)
  Radius = 3
FEATURE [Part::Cylinder] Cylinder636  label="Válec636"
  Angle = 360
  AttacherType = Attacher::AttachEngine3D
  Height = 3
  Placement = pos=(44,3.4e-14,10) rot=(0,0,1;3.53429rad)
  Radius = 3
FEATURE [Part::Compound] Compound671
  Links = -> [Cylinder687,Cylinder634,Cylinder635,Cylinder636]
  Placement = pos=(0,0,18) rot=(0,0,1;0rad)
FEATURE [Part::Box] Box329  label="Krychle329"
  AttacherType = Attacher::AttachEngine3D
  Height = 8
  Length = 3
  Placement = pos=(-51,14,23) rot=(0,0,1;0rad)
  Width = 16
FEATURE [Part::Box] Box330  label="Krychle330"
  AttacherType = Attacher::AttachEngine3D
  Height = 8
  Length = 3
  Placement = pos=(48,14,23) rot=(0,0,1;0rad)
  Width = 16
FEATURE [Part::Cylinder] Cylinder637  label="Válec637"
  Angle = 360
  AttacherType = Attacher::AttachEngine3D
  Height = 3
  Placement = pos=(-48,61,0) rot=(0,0,1;0rad)
  Radius = 3
FEATURE [Part::Cylinder] Cylinder688  label="Válec688"
  Angle = 360
  AttacherType = Attacher::AttachEngine3D
  Height = 3
  Placement = pos=(-22,61,0) rot=(0,0,1;0rad)
  Radius = 3
FEATURE [Part::Cylinder] Cylinder689  label="Válec689"
  Angle = 360
  AttacherType = Attacher::AttachEngine3D
  Height = 3
  Placement = pos=(48,61,0) rot=(0,0,1;0rad)
  Radius = 3
FEATURE [Part::Cylinder] Cylinder640  label="Válec640"
  Angle = 360
  AttacherType = Attacher::AttachEngine3D
  Height = 3
  Placement = pos=(22,61,0) rot=(0,0,1;0rad)
  Radius = 3
FEATURE [Part::Cylinder] Cylinder641  label="Válec641"
  Angle = 360
  AttacherType = Attacher::AttachEngine3D
  Height = 30
  Placement = pos=(-31.1127,-31.1127,10) rot=(0,0,1;1.1781rad)
  Radius = 1.5
FEATURE [Part::Cylinder] Cylinder642  label="Válec642"
  Angle = 360
  AttacherType = Attacher::AttachEngine3D
  Height = 30
  Placement = pos=(31.1127,-31.1127,10) rot=(0,0,1;2.74889rad)
  Radius = 1.5
FEATURE [Part::Cylinder] Cylinder643  label="Válec643"
  Angle = 360
  AttacherType = Attacher::AttachEngine3D
  Height = 3
  Placement = pos=(-31.1127,-31.1127,10) rot=(0,0,1;1.1781rad)
  Radius = 3
FEATURE [Part::Cylinder] Cylinder644  label="Válec644"
  Angle = 360
  AttacherType = Attacher::AttachEngine3D
  Height = 3
  Placement = pos=(31.1127,-31.1127,10) rot=(0,0,1;2.74889rad)
  Radius = 3
FEATURE [Part::Compound] Compound672
  Links = -> [Cylinder637,Cylinder688,Cylinder689,Cylinder640]
  Placement = pos=(0,0,28) rot=(0,0,1;0rad)
FEATURE [Part::Compound] Compound673
  Links = -> [Cylinder641,Cylinder642]
FEATURE [Part::Compound] Compound674
  Links = -> [Cylinder643,Cylinder644]
  Placement = pos=(0,0,18) rot=(0,0,1;0rad)
FEATURE [Part::Chamfer] Chamfer035
  Base = -> Box329
  Edges = 1 edges r=2.9: [Edge1]
FEATURE [Part::Chamfer] Chamfer037
  Base = -> Box330
  Edges = 1 edges r=2.9: [Edge5]
FEATURE [Part::Cut] Cut289
  Base = -> Cut288
  Tool = -> Compound671
FEATURE [Part::Cut] Cut304
  Base = -> Cut289
  Tool = -> Compound674
FEATURE [Part::Cut] Cut305
  Base = -> Cut304
  Tool = -> Compound672
FEATURE [Part::Cut] Cut306
  Base = -> Cut305
  Tool = -> Compound673
FEATURE [Part::Chamfer] Chamfer036
  Base = -> Cut306
  Edges = 2 edges r=2: [Edge104,Edge164]
FEATURE [Part::Fillet] Fillet008
  Base = -> Chamfer036
  Edges = 2 edges r=3: [Edge6,Edge219]
FEATURE [Part::Compound] Compound675  label="J-max_bear-cover"
  Links = -> [Tube035,Chamfer035,Chamfer037,Fillet008]
  Placement = pos=(0,0,-24) rot=(0,1,0;3.14159rad)
FEATURE [Part::Box] Box331  label="Krychle331"
  AttacherType = Attacher::AttachEngine3D
  Height = 20
  Length = 20
  Placement = pos=(-45,28,8) rot=(0,0,1;0rad)
  Width = 200
FEATURE [Part::Box] Box332  label="Krychle332"
  AttacherType = Attacher::AttachEngine3D
  Height = 20
  Length = 20
  Placement = pos=(25,28,8) rot=(0,0,1;0rad)
  Width = 200
FEATURE [Part::Compound] Compound676
  Links = -> [Box332,Box331]
  Placement = pos=(0,0,-60) rot=(0,0,1;0rad)
FEATURE [Part::Box] Box333  label="Krychle333"
  AttacherType = Attacher::AttachEngine3D
  Height = 4
  Length = 90
  Placement = pos=(-45,80,-56) rot=(0,0,1;0rad)
  Width = 16
FEATURE [Part::Cylinder] Cylinder774  label="Válec774"
  Angle = 360
  AttacherType = Attacher::AttachEngine3D
  Height = 20
  Placement = pos=(15.75,114,38.52) rot=(0,0.707107,0.707107;3.14159rad)
  Radius = 1.5
FEATURE [Part::Cylinder] Cylinder776  label="Válec776"
  Angle = 360
  AttacherType = Attacher::AttachEngine3D
  Height = 20
  Placement = pos=(15.75,114,59.48) rot=(0,0.707107,0.707107;3.14159rad)
  Radius = 1.5
FEATURE [Part::Compound] Compound536
  Links = -> [Cylinder774,Cylinder776]
  Placement = pos=(-49,0,-96) rot=(0.57735,0.57735,0.57735;2.0944rad)
FEATURE [Part::Box] Box636  label="Krychle636"
  AttacherType = Attacher::AttachEngine3D
  Height = 3
  Length = 16
  Placement = pos=(-33.45,-27.55,31) rot=(0,0,1;0rad)
  Width = 8
FEATURE [Part::Cylinder] Cylinder1598  label="Válec1598"
  Angle = 360
  AttacherType = Attacher::AttachEngine3D
  Height = 4
  Placement = pos=(23.55,23.55,26) rot=(0,0,1;0rad)
  Radius = 5
FEATURE [Part::Cylinder] Cylinder1599  label="Válec1599"
  Angle = 360
  AttacherType = Attacher::AttachEngine3D
  Height = 30
  Placement = pos=(-1.2e-14,-16,2) rot=(0,0,1;1.96349rad)
  Radius = 1.5
FEATURE [Part::Cylinder] Cylinder1600  label="Válec1600"
  Angle = 360
  AttacherType = Attacher::AttachEngine3D
  Height = 20
  Placement = pos=(0,0,15) rot=(0,0,1;0rad)
  Radius = 12
FEATURE [Part::Cylinder] Cylinder1601  label="Válec1601"
  Angle = 360
  AttacherType = Attacher::AttachEngine3D
  Height = 3
  Placement = pos=(2e-15,16,2) rot=(0,0,-1;1.1781rad)
  Radius = 3
FEATURE [Part::Box] Box637  label="Krychle637"
  AttacherType = Attacher::AttachEngine3D
  Height = 3
  Length = 16
  Placement = pos=(17.55,19.55,31) rot=(0,0,1;0rad)
  Width = 8
FEATURE [Part::Cylinder] Cylinder1602  label="Válec1602"
  Angle = 360
  AttacherType = Attacher::AttachEngine3D
  Height = 20
  Placement = pos=(23.55,23.55,20) rot=(0,0,1;0rad)
  Radius = 2.5
FEATURE [Part::Cylinder] Cylinder1603  label="Válec1603"
  Angle = 360
  AttacherType = Attacher::AttachEngine3D
  Height = 30
  Placement = pos=(-16,7e-15,2) rot=(0,0,1;0.392699rad)
  Radius = 1.5
FEATURE [Part::Cylinder] Cylinder1604  label="Válec1604"
  Angle = 360
  AttacherType = Attacher::AttachEngine3D
  Height = 20
  Placement = pos=(-23.55,23.55,20) rot=(0,0,1;0rad)
  Radius = 2.5
FEATURE [Part::Cylinder] Cylinder1605  label="Válec1605"
  Angle = 360
  AttacherType = Attacher::AttachEngine3D
  Height = 4
  Placement = pos=(23.55,-23.55,26) rot=(0,0,1;0rad)
  Radius = 5
FEATURE [Part::Box] Box638  label="Krychle638"
  AttacherType = Attacher::AttachEngine3D
  Height = 8
  Length = 64
  Placement = pos=(-32,-32,26) rot=(0,0,1;0rad)
  Width = 64
FEATURE [Part::Cylinder] Cylinder1606  label="Válec1606"
  Angle = 360
  AttacherType = Attacher::AttachEngine3D
  Height = 3
  Placement = pos=(16,0,2) rot=(0,0,1;3.53429rad)
  Radius = 3
FEATURE [Part::Box] Box639  label="Krychle639"
  AttacherType = Attacher::AttachEngine3D
  Height = 3
  Length = 16
  Placement = pos=(-33.45,19.55,31) rot=(0,0,1;0rad)
  Width = 8
FEATURE [Part::Cylinder] Cylinder1607  label="Válec1607"
  Angle = 360
  AttacherType = Attacher::AttachEngine3D
  Height = 20
  Placement = pos=(23.55,-23.55,20) rot=(0,0,1;0rad)
  Radius = 2.5
FEATURE [Part::Cylinder] Cylinder1608  label="Válec1608"
  Angle = 360
  AttacherType = Attacher::AttachEngine3D
  Height = 20
  Placement = pos=(-23.55,-23.55,20) rot=(0,0,1;0rad)
  Radius = 2.5
FEATURE [Part::Compound] Compound798
  Links = -> [Cylinder1602,Cylinder1604,Cylinder1608,Cylinder1607]
FEATURE [Part::Box] Box640  label="Krychle640"
  AttacherType = Attacher::AttachEngine3D
  Height = 3
  Length = 16
  Placement = pos=(17.55,-27.55,31) rot=(0,0,1;0rad)
  Width = 8
FEATURE [Part::Cylinder] Cylinder1609  label="Válec1609"
  Angle = 360
  AttacherType = Attacher::AttachEngine3D
  Height = 3
  Placement = pos=(-16,7e-15,2) rot=(0,0,1;0.392699rad)
  Radius = 3
FEATURE [Part::Compound] Compound800
  Links = -> [Box637,Box640,Box639,Box636]
FEATURE [Part::Cylinder] Cylinder1610  label="Válec1610"
  Angle = 360
  AttacherType = Attacher::AttachEngine3D
  Height = 4
  Placement = pos=(-23.55,-23.55,26) rot=(0,0,1;0rad)
  Radius = 5
FEATURE [Part::Cylinder] Cylinder1611  label="Válec1611"
  Angle = 360
  AttacherType = Attacher::AttachEngine3D
  Height = 3
  Placement = pos=(-1.2e-14,-16,2) rot=(0,0,1;1.96349rad)
  Radius = 3
FEATURE [Part::Compound] Compound801
  Links = -> [Cylinder1611,Cylinder1609,Cylinder1601,Cylinder1606]
  Placement = pos=(0,0,29) rot=(0,0,1;0.785398rad)
FEATURE [Part::Cylinder] Cylinder1612  label="Válec1612"
  Angle = 360
  AttacherType = Attacher::AttachEngine3D
  Height = 4
  Placement = pos=(-23.55,23.55,26) rot=(0,0,1;0rad)
  Radius = 5
FEATURE [Part::Compound] Compound799
  Links = -> [Cylinder1610,Cylinder1598,Cylinder1605,Cylinder1612]
  Placement = pos=(0,0,-50) rot=(0,0,1;0rad)
FEATURE [Part::Cylinder] Cylinder1613  label="Válec1613"
  Angle = 360
  AttacherType = Attacher::AttachEngine3D
  Height = 30
  Placement = pos=(2e-15,16,2) rot=(0,0,-1;1.1781rad)
  Radius = 1.5
FEATURE [Part::Cylinder] Cylinder1614  label="Válec1614"
  Angle = 360
  AttacherType = Attacher::AttachEngine3D
  Height = 30
  Placement = pos=(16,0,2) rot=(0,0,1;3.53429rad)
  Radius = 1.5
FEATURE [Part::Compound] Compound802
  Links = -> [Cylinder1599,Cylinder1603,Cylinder1613,Cylinder1614]
  Placement = pos=(0,0,14) rot=(0,0,1;0.785398rad)
FEATURE [Part::Cut] Cut173
  Base = -> Box638
  Tool = -> Compound802
FEATURE [Part::Cut] Cut174
  Base = -> Cut173
  Tool = -> Compound801
FEATURE [Part::Cut] Cut177
  Base = -> Cut174
  Tool = -> Compound798
FEATURE [Part::Cut] Cut175
  Base = -> Cut177
  Tool = -> Compound799
FEATURE [Part::Cut] Cut176
  Base = -> Cut175
  Tool = -> Cylinder1600
FEATURE [Part::Cut] Cut178
  Base = -> Cut176
  Tool = -> Compound800
FEATURE [Part::Cut] Cut179
  Base = -> Cut178
  Tool = -> Compound536
FEATURE [Part::Box] Box641  label="Krychle641"
  AttacherType = Attacher::AttachEngine3D
  Height = 9
  Length = 28.8
  Placement = pos=(-14.4,-15.34,34) rot=(0,0,1;0rad)
  Width = 43.38
FEATURE [Part::Cylinder] Cylinder1615  label="Válec1615"
  Angle = 360
  AttacherType = Attacher::AttachEngine3D
  Height = 100
  Radius = 4
FEATURE [Part::Cut] Cut307
  Base = -> Box641
  Placement = pos=(0,90,-86) rot=(0,0,1;0rad)
  Tool = -> Cylinder1615
FEATURE [Part::Box] Box642  label="Krychle642"
  AttacherType = Attacher::AttachEngine3D
  Height = 9
  Length = 28.8
  Placement = pos=(-14.4,-15.34,34) rot=(0,0,1;0rad)
  Width = 34.21
FEATURE [Part::Cylinder] Cylinder1616  label="Válec1616"
  Angle = 360
  AttacherType = Attacher::AttachEngine3D
  Height = 100
  Radius = 4
FEATURE [Part::Cut] Cut308
  Base = -> Box642
  Placement = pos=(0,90,-83) rot=(0,0,1;0rad)
  Tool = -> Cylinder1616
FEATURE [Part::Cylinder] Cylinder1617  label="Válec1617"
  Angle = 360
  AttacherType = Attacher::AttachEngine3D
  Height = 5
  Placement = pos=(0,90,-54) rot=(0,0,1;0rad)
  Radius = 5
FEATURE [Part::Box] Box643  label="Krychle643"
  AttacherType = Attacher::AttachEngine3D
  Height = 4
  Length = 90
  Placement = pos=(-45,80,-56) rot=(0,0,1;0rad)
  Width = 20
FEATURE [Part::Box] Box644  label="Krychle644"
  AttacherType = Attacher::AttachEngine3D
  Height = 4
  Length = 90
  Placement = pos=(-45,80,-32) rot=(0,0,1;0rad)
  Width = 20
FEATURE [Part::Cylinder] Cylinder1618  label="Válec1618"
  Angle = 360
  AttacherType = Attacher::AttachEngine3D
  Height = 6
  Placement = pos=(0,90,-40) rot=(0,0,1;0rad)
  Radius = 8
FEATURE [Part::Cylinder] Cylinder1619  label="Válec1619"
  Angle = 360
  AttacherType = Attacher::AttachEngine3D
  Height = 48
  Placement = pos=(0,90,-55) rot=(0,0,1;0rad)
  Radius = 3
FEATURE [Part::Box] Box645  label="Krychle645"
  AttacherType = Attacher::AttachEngine3D
  Height = 3
  Length = 42
  Placement = pos=(-21,80,-52) rot=(0,0,1;0rad)
  Width = 32
FEATURE [Part::Cylinder] Cylinder1620  label="Válec1620"
  Angle = 360
  AttacherType = Attacher::AttachEngine3D
  Height = 4
  Placement = pos=(0,90,-53) rot=(0,0,1;0rad)
  Radius = 5
FEATURE [Part::Cut] Cut309
  Base = -> Box645
  Tool = -> Cylinder1620
FEATURE [Part::Cut] Cut310
  Base = -> Box643
  Tool = -> Cylinder1617
FEATURE [Part::Box] Box646  label="Krychle646"
  AttacherType = Attacher::AttachEngine3D
  Height = 9
  Length = 28.8
  Placement = pos=(-14.4,-15.34,34) rot=(0,0,1;0rad)
  Width = 34.21
FEATURE [Part::Compound] Compound803
  Links = -> [Box646]
  Placement = pos=(0,90,-83) rot=(0,0,1;0rad)
FEATURE [Part::Box] Box647  label="Krychle647"
  AttacherType = Attacher::AttachEngine3D
  Height = 9
  Length = 42
  Placement = pos=(-21,80,-49) rot=(0,0,1;0rad)
  Width = 20
FEATURE [Part::Cut] Cut311
  Base = -> Box647
  Placement = pos=(0,0,1) rot=(0,0,1;0rad)
  Tool = -> Compound803
FEATURE [Part::Box] Box648  label="Krychle648"
  AttacherType = Attacher::AttachEngine3D
  Height = 2
  Length = 6
  Placement = pos=(-21,82,-56) rot=(0,0,1;0rad)
  Width = 6
FEATURE [Part::Box] Box649  label="Krychle649"
  AttacherType = Attacher::AttachEngine3D
  Height = 2
  Length = 6
  Placement = pos=(-21,92,-56) rot=(0,0,1;0rad)
  Width = 6
FEATURE [Part::Box] Box650  label="Krychle650"
  AttacherType = Attacher::AttachEngine3D
  Height = 2
  Length = 6
  Placement = pos=(15,82,-56) rot=(0,0,1;0rad)
  Width = 6
FEATURE [Part::Box] Box651  label="Krychle651"
  AttacherType = Attacher::AttachEngine3D
  Height = 2
  Length = 6
  Placement = pos=(15,92,-56) rot=(0,0,1;0rad)
  Width = 6
FEATURE [Part::Cylinder] Cylinder1621  label="Válec1621"
  Angle = 360
  AttacherType = Attacher::AttachEngine3D
  Height = 60
  Placement = pos=(18,95,-57) rot=(0,0,1;0rad)
  Radius = 1.5
FEATURE [Part::Cylinder] Cylinder1622  label="Válec1622"
  Angle = 360
  AttacherType = Attacher::AttachEngine3D
  Height = 60
  Placement = pos=(18,85,-57) rot=(0,0,1;0rad)
  Radius = 1.5
FEATURE [Part::Cylinder] Cylinder1623  label="Válec1623"
  Angle = 360
  AttacherType = Attacher::AttachEngine3D
  Height = 60
  Placement = pos=(-18,85,-57) rot=(0,0,1;0rad)
  Radius = 1.5
FEATURE [Part::Cylinder] Cylinder1624  label="Válec1624"
  Angle = 360
  AttacherType = Attacher::AttachEngine3D
  Height = 60
  Placement = pos=(-18,95,-57) rot=(0,0,1;0rad)
  Radius = 1.5
FEATURE [Part::Compound] Compound804
  Links = -> [Cut179]
  Placement = pos=(0,90,-83) rot=(0,0,1;0rad)
FEATURE [Part::Box] Box652  label="Krychle652"
  AttacherType = Attacher::AttachEngine3D
  Height = 6
  Length = 42
  Placement = pos=(-21,80,-38) rot=(0,0,1;0rad)
  Width = 20
FEATURE [Part::Cylinder] Cylinder1625  label="Válec1625"
  Angle = 360
  AttacherType = Attacher::AttachEngine3D
  Height = 48
  Placement = pos=(0,90,-55) rot=(0,0,1;0rad)
  Radius = 3
FEATURE [Part::Cut] Cut312
  Base = -> Box652
  Tool = -> Cylinder1625
FEATURE [Part::Cut] Cut313
  Base = -> Box644
  Tool = -> Cylinder1619
FEATURE [Part::Cylinder] Cylinder1626  label="Válec1626"
  Angle = 360
  AttacherType = Attacher::AttachEngine3D
  Height = 5
  Placement = pos=(0,90,-38) rot=(0,0,1;0rad)
  Radius = 5
FEATURE [Part::Cut] Cut314
  Base = -> Cut312
  Tool = -> Cylinder1626
FEATURE [Part::Box] Box653  label="Krychle653"
  AttacherType = Attacher::AttachEngine3D
  Height = 20
  Length = 28.8
  Placement = pos=(-14.4,-15.34,34) rot=(0,0,1;0rad)
  Width = 34.21
FEATURE [Part::Box] Box654  label="Krychle654"
  AttacherType = Attacher::AttachEngine3D
  Height = 24
  Length = 42
  Placement = pos=(-21,80,-49) rot=(0,0,1;0rad)
  Width = 20
FEATURE [Part::Compound] Compound805
  Links = -> [Box653]
  Placement = pos=(0,90,-83) rot=(0,0,1;0rad)
FEATURE [Part::Cut] Cut315
  Base = -> Box654
  Placement = pos=(0,0,21) rot=(0,0,1;0rad)
  Tool = -> Compound805
FEATURE [Part::Cylinder] Cylinder1627  label="Válec1627"
  Angle = 360
  AttacherType = Attacher::AttachEngine3D
  Height = 48
  Placement = pos=(0,90,-55) rot=(0,0,1;0rad)
  Radius = 2.5
FEATURE [Part::Cut] Cut316
  Base = -> Cut315
  Tool = -> Cylinder1627
FEATURE [Part::Box] Box655  label="Krychle655"
  AttacherType = Attacher::AttachEngine3D
  Height = 1
  Length = 42
  Placement = pos=(-21,80,-39) rot=(0,0,1;0rad)
  Width = 20
FEATURE [Part::Box] Box656  label="Krychle656"
  AttacherType = Attacher::AttachEngine3D
  Height = 1
  Length = 42
  Placement = pos=(-21,80,-49) rot=(0,0,1;0rad)
  Width = 32
FEATURE [Part::Cylinder] Cylinder1628  label="Válec1628"
  Angle = 360
  AttacherType = Attacher::AttachEngine3D
  Height = 48
  Placement = pos=(0,90,-55) rot=(0,0,1;0rad)
  Radius = 7
FEATURE [Part::Cylinder] Cylinder1629  label="Válec1629"
  Angle = 360
  AttacherType = Attacher::AttachEngine3D
  Height = 48
  Placement = pos=(0,90,-55) rot=(0,0,1;0rad)
  Radius = 4
FEATURE [Part::Cut] Cut317
  Base = -> Box655
  Tool = -> Cylinder1628
FEATURE [Part::Cut] Cut318
  Base = -> Box656
  Tool = -> Cylinder1629
FEATURE [Part::Chamfer] Chamfer038
  Base = -> Cut316
  Edges = 2 edges r=6: [Edge6,Edge8]
FEATURE [Part::Compound] Compound806
  Links = -> [Cylinder1621,Cylinder1622,Cylinder1623,Cylinder1624]
FEATURE [Part::Compound] Compound807
  Links = -> [Box648,Box649,Box650,Box651]
  Placement = pos=(0,0,21) rot=(0,0,1;0rad)
FEATURE [Part::Cylinder] Cylinder1630  label="Válec1630"
  Angle = 360
  AttacherType = Attacher::AttachEngine3D
  Height = 60
  Placement = pos=(18,95,-57) rot=(0,0,1;0rad)
  Radius = 1.5
FEATURE [Part::Cylinder] Cylinder1631  label="Válec1631"
  Angle = 360
  AttacherType = Attacher::AttachEngine3D
  Height = 60
  Placement = pos=(18,85,-57) rot=(0,0,1;0rad)
  Radius = 1.5
FEATURE [Part::Cylinder] Cylinder1632  label="Válec1632"
  Angle = 360
  AttacherType = Attacher::AttachEngine3D
  Height = 60
  Placement = pos=(-18,85,-57) rot=(0,0,1;0rad)
  Radius = 1.5
FEATURE [Part::Cylinder] Cylinder1633  label="Válec1633"
  Angle = 360
  AttacherType = Attacher::AttachEngine3D
  Height = 60
  Placement = pos=(-18,95,-57) rot=(0,0,1;0rad)
  Radius = 1.5
FEATURE [Part::Compound] Compound808
  Links = -> [Cylinder1630,Cylinder1631,Cylinder1632,Cylinder1633]
FEATURE [Part::Cut] Cut319
  Base = -> Cut314
  Tool = -> Compound807
FEATURE [Part::Cylinder] Cylinder1634  label="Válec1634"
  Angle = 360
  AttacherType = Attacher::AttachEngine3D
  Height = 60
  Placement = pos=(18,95,-57) rot=(0,0,1;0rad)
  Radius = 1.5
FEATURE [Part::Cylinder] Cylinder1635  label="Válec1635"
  Angle = 360
  AttacherType = Attacher::AttachEngine3D
  Height = 60
  Placement = pos=(18,85,-57) rot=(0,0,1;0rad)
  Radius = 1.5
FEATURE [Part::Cylinder] Cylinder1636  label="Válec1636"
  Angle = 360
  AttacherType = Attacher::AttachEngine3D
  Height = 60
  Placement = pos=(-18,85,-57) rot=(0,0,1;0rad)
  Radius = 1.5
FEATURE [Part::Cylinder] Cylinder1637  label="Válec1637"
  Angle = 360
  AttacherType = Attacher::AttachEngine3D
  Height = 60
  Placement = pos=(-18,95,-57) rot=(0,0,1;0rad)
  Radius = 1.5
FEATURE [Part::Compound] Compound809
  Links = -> [Cylinder1634,Cylinder1635,Cylinder1636,Cylinder1637]
  Placement = pos=(0,0,-16) rot=(0,0,1;0rad)
FEATURE [Part::Cut] Cut320
  Base = -> Cut318
  Tool = -> Compound806
FEATURE [Part::Cut] Cut321
  Base = -> Cut319
  Tool = -> Compound808
FEATURE [Part::Cylinder] Cylinder1638  label="Válec1638"
  Angle = 360
  AttacherType = Attacher::AttachEngine3D
  Height = 60
  Placement = pos=(18,95,-57) rot=(0,0,1;0rad)
  Radius = 1.5
FEATURE [Part::Cylinder] Cylinder1639  label="Válec1639"
  Angle = 360
  AttacherType = Attacher::AttachEngine3D
  Height = 60
  Placement = pos=(18,85,-57) rot=(0,0,1;0rad)
  Radius = 1.5
FEATURE [Part::Cylinder] Cylinder1640  label="Válec1640"
  Angle = 360
  AttacherType = Attacher::AttachEngine3D
  Height = 60
  Placement = pos=(-18,85,-57) rot=(0,0,1;0rad)
  Radius = 1.5
FEATURE [Part::Cylinder] Cylinder1641  label="Válec1641"
  Angle = 360
  AttacherType = Attacher::AttachEngine3D
  Height = 60
  Placement = pos=(-18,95,-57) rot=(0,0,1;0rad)
  Radius = 1.5
FEATURE [Part::Compound] Compound810
  Links = -> [Cylinder1638,Cylinder1639,Cylinder1640,Cylinder1641]
FEATURE [Part::Cut] Cut322  label="J-max_encoder-washer"
  Base = -> Cut317
  Tool = -> Compound810
FEATURE [Part::Cylinder] Cylinder1642  label="Válec1642"
  Angle = 360
  AttacherType = Attacher::AttachEngine3D
  Height = 60
  Placement = pos=(18,95,-57) rot=(0,0,1;0rad)
  Radius = 1.5
FEATURE [Part::Cylinder] Cylinder1643  label="Válec1643"
  Angle = 360
  AttacherType = Attacher::AttachEngine3D
  Height = 60
  Placement = pos=(18,85,-57) rot=(0,0,1;0rad)
  Radius = 1.5
FEATURE [Part::Cylinder] Cylinder1644  label="Válec1644"
  Angle = 360
  AttacherType = Attacher::AttachEngine3D
  Height = 60
  Placement = pos=(-18,85,-57) rot=(0,0,1;0rad)
  Radius = 1.5
FEATURE [Part::Cylinder] Cylinder1645  label="Válec1645"
  Angle = 360
  AttacherType = Attacher::AttachEngine3D
  Height = 60
  Placement = pos=(-18,95,-57) rot=(0,0,1;0rad)
  Radius = 1.5
FEATURE [Part::Compound] Compound811
  Links = -> [Cylinder1642,Cylinder1643,Cylinder1644,Cylinder1645]
FEATURE [Part::Cut] Cut323
  Base = -> Cut311
  Tool = -> Compound811
FEATURE [Part::Cylinder] Cylinder1646  label="Válec1646"
  Angle = 360
  AttacherType = Attacher::AttachEngine3D
  Height = 60
  Placement = pos=(18,95,-57) rot=(0,0,1;0rad)
  Radius = 1.5
FEATURE [Part::Cylinder] Cylinder1647  label="Válec1647"
  Angle = 360
  AttacherType = Attacher::AttachEngine3D
  Height = 60
  Placement = pos=(18,85,-57) rot=(0,0,1;0rad)
  Radius = 1.5
FEATURE [Part::Cylinder] Cylinder1648  label="Válec1648"
  Angle = 360
  AttacherType = Attacher::AttachEngine3D
  Height = 60
  Placement = pos=(-18,85,-57) rot=(0,0,1;0rad)
  Radius = 1.5
FEATURE [Part::Cylinder] Cylinder1649  label="Válec1649"
  Angle = 360
  AttacherType = Attacher::AttachEngine3D
  Height = 60
  Placement = pos=(-18,95,-57) rot=(0,0,1;0rad)
  Radius = 1.5
FEATURE [Part::Compound] Compound812
  Links = -> [Cylinder1646,Cylinder1647,Cylinder1648,Cylinder1649]
FEATURE [Part::Cut] Cut324
  Base = -> Cut313
  Tool = -> Compound812
FEATURE [Part::Cut] Cut325
  Base = -> Chamfer038
  Tool = -> Compound809
FEATURE [Part::Cylinder] Cylinder1650  label="Válec1650"
  Angle = 360
  AttacherType = Attacher::AttachEngine3D
  Height = 60
  Placement = pos=(18,95,-57) rot=(0,0,1;0rad)
  Radius = 1.5
FEATURE [Part::Cylinder] Cylinder1651  label="Válec1651"
  Angle = 360
  AttacherType = Attacher::AttachEngine3D
  Height = 60
  Placement = pos=(18,85,-57) rot=(0,0,1;0rad)
  Radius = 1.5
FEATURE [Part::Cylinder] Cylinder1652  label="Válec1652"
  Angle = 360
  AttacherType = Attacher::AttachEngine3D
  Height = 60
  Placement = pos=(-18,85,-57) rot=(0,0,1;0rad)
  Radius = 1.5
FEATURE [Part::Cylinder] Cylinder1653  label="Válec1653"
  Angle = 360
  AttacherType = Attacher::AttachEngine3D
  Height = 60
  Placement = pos=(-18,95,-57) rot=(0,0,1;0rad)
  Radius = 1.5
FEATURE [Part::Compound] Compound813
  Links = -> [Cylinder1650,Cylinder1651,Cylinder1652,Cylinder1653]
FEATURE [Part::Cut] Cut326
  Base = -> Cut310
  Tool = -> Compound813
FEATURE [Part::Cylinder] Cylinder1654  label="Válec1654"
  Angle = 360
  AttacherType = Attacher::AttachEngine3D
  Height = 60
  Placement = pos=(18,95,-57) rot=(0,0,1;0rad)
  Radius = 1.5
FEATURE [Part::Cylinder] Cylinder1655  label="Válec1655"
  Angle = 360
  AttacherType = Attacher::AttachEngine3D
  Height = 60
  Placement = pos=(18,85,-57) rot=(0,0,1;0rad)
  Radius = 1.5
FEATURE [Part::Cylinder] Cylinder1656  label="Válec1656"
  Angle = 360
  AttacherType = Attacher::AttachEngine3D
  Height = 60
  Placement = pos=(-18,85,-57) rot=(0,0,1;0rad)
  Radius = 1.5
FEATURE [Part::Cylinder] Cylinder1657  label="Válec1657"
  Angle = 360
  AttacherType = Attacher::AttachEngine3D
  Height = 60
  Placement = pos=(-18,95,-57) rot=(0,0,1;0rad)
  Radius = 1.5
FEATURE [Part::Compound] Compound814
  Links = -> [Cylinder1654,Cylinder1655,Cylinder1656,Cylinder1657]
FEATURE [Part::Cut] Cut327
  Base = -> Cut309
  Tool = -> Compound814
FEATURE [Part::Cylinder] Cylinder1658  label="Válec1658"
  Angle = 360
  AttacherType = Attacher::AttachEngine3D
  Height = 3
  Placement = pos=(18,95,-57) rot=(0,0,1;0rad)
  Radius = 3
FEATURE [Part::Cylinder] Cylinder1659  label="Válec1659"
  Angle = 360
  AttacherType = Attacher::AttachEngine3D
  Height = 3
  Placement = pos=(18,85,-57) rot=(0,0,1;0rad)
  Radius = 3
FEATURE [Part::Cylinder] Cylinder1660  label="Válec1660"
  Angle = 360
  AttacherType = Attacher::AttachEngine3D
  Height = 3
  Placement = pos=(-18,85,-57) rot=(0,0,1;0rad)
  Radius = 3
FEATURE [Part::Cylinder] Cylinder1661  label="Válec1661"
  Angle = 360
  AttacherType = Attacher::AttachEngine3D
  Height = 3
  Placement = pos=(-18,95,-57) rot=(0,0,1;0rad)
  Radius = 3
FEATURE [Part::Compound] Compound815
  Links = -> [Cylinder1658,Cylinder1659,Cylinder1660,Cylinder1661]
FEATURE [Part::Cut] Cut328
  Base = -> Cut326
  Tool = -> Compound815
FEATURE [Part::Chamfer] Chamfer039
  Base = -> Cut325
  Edges = 2 edges r=4: [Edge17,Edge20]
FEATURE [Part::Cylinder] Cylinder1662  label="Válec1662"
  Angle = 360
  AttacherType = Attacher::AttachEngine3D
  Height = 5
  Placement = pos=(35,90,-59) rot=(0,0,1;0rad)
  Radius = 5
FEATURE [Part::Cylinder] Cylinder1663  label="Válec1663"
  Angle = 360
  AttacherType = Attacher::AttachEngine3D
  Height = 5
  Placement = pos=(-35,90,-59) rot=(0,0,1;0rad)
  Radius = 5
FEATURE [Part::Cylinder] Cylinder1664  label="Válec1664"
  Angle = 360
  AttacherType = Attacher::AttachEngine3D
  Height = 20
  Placement = pos=(35,90,-59) rot=(0,0,1;0rad)
  Radius = 2.5
FEATURE [Part::Cylinder] Cylinder1665  label="Válec1665"
  Angle = 360
  AttacherType = Attacher::AttachEngine3D
  Height = 20
  Placement = pos=(-35,90,-59) rot=(0,0,1;0rad)
  Radius = 2.5
FEATURE [Part::Compound] Compound816
  Links = -> [Cylinder1662,Cylinder1663]
FEATURE [Part::Compound] Compound817
  Links = -> [Cylinder1664,Cylinder1665]
FEATURE [Part::Cut] Cut329
  Base = -> Cut328
  Tool = -> Compound816
FEATURE [Part::Cut] Cut330
  Base = -> Cut329
  Tool = -> Compound817
FEATURE [Part::Cylinder] Cylinder1666  label="Válec1666"
  Angle = 360
  AttacherType = Attacher::AttachEngine3D
  Height = 5
  Placement = pos=(35,90,-59) rot=(0,0,1;0rad)
  Radius = 5
FEATURE [Part::Cylinder] Cylinder1667  label="Válec1667"
  Angle = 360
  AttacherType = Attacher::AttachEngine3D
  Height = 5
  Placement = pos=(-35,90,-59) rot=(0,0,1;0rad)
  Radius = 5
FEATURE [Part::Compound] Compound818
  Links = -> [Cylinder1666,Cylinder1667]
  Placement = pos=(0,0,29) rot=(0,0,1;0rad)
FEATURE [Part::Cylinder] Cylinder1668  label="Válec1668"
  Angle = 360
  AttacherType = Attacher::AttachEngine3D
  Height = 20
  Placement = pos=(35,90,-59) rot=(0,0,1;0rad)
  Radius = 2.5
FEATURE [Part::Cylinder] Cylinder1669  label="Válec1669"
  Angle = 360
  AttacherType = Attacher::AttachEngine3D
  Height = 20
  Placement = pos=(-35,90,-59) rot=(0,0,1;0rad)
  Radius = 2.5
FEATURE [Part::Compound] Compound819
  Links = -> [Cylinder1668,Cylinder1669]
  Placement = pos=(0,0,18) rot=(0,0,1;0rad)
FEATURE [Part::Cut] Cut331
  Base = -> Cut324
  Tool = -> Compound818
FEATURE [Part::Cut] Cut332
  Base = -> Cut331
  Tool = -> Compound819
FEATURE [Part::Chamfer] Chamfer040
  Base = -> Cut330
  Edges = 2 edges r=4: [Edge3,Edge18]
FEATURE [Part::Chamfer] Chamfer041
  Base = -> Chamfer040
  Edges = 2 edges r=2: [Edge3,Edge21]
FEATURE [Part::Chamfer] Chamfer042
  Base = -> Cut332
  Edges = 2 edges r=4: [Edge3,Edge18]
FEATURE [Part::Chamfer] Chamfer043
  Base = -> Chamfer042
  Edges = 2 edges r=2: [Edge1,Edge6]
FEATURE [Part::Chamfer] Chamfer044
  Base = -> Chamfer039
  Edges = 2 edges r=2: [Edge14,Edge35]
FEATURE [Part::Cylinder] Cylinder1670  label="Válec1670"
  Angle = 360
  AttacherType = Attacher::AttachEngine3D
  Height = 20
  Placement = pos=(15.75,114,39.48) rot=(0,0.707107,0.707107;3.14159rad)
  Radius = 1.5
FEATURE [Part::Cylinder] Cylinder1671  label="Válec1671"
  Angle = 360
  AttacherType = Attacher::AttachEngine3D
  Height = 20
  Placement = pos=(15.75,114,58.525) rot=(0,0.707107,0.707107;3.14159rad)
  Radius = 1.5
FEATURE [Part::Compound] Compound820
  Links = -> [Cylinder1670,Cylinder1671]
  Placement = pos=(-49,0,-96) rot=(0.57735,0.57735,0.57735;2.0944rad)
FEATURE [Part::Compound] Compound821
  Links = -> [Compound820]
  Placement = pos=(0,74,-80) rot=(0,0,1;0rad)
FEATURE [Part::Cylinder] Cylinder1672  label="Válec1672"
  Angle = 360
  AttacherType = Attacher::AttachEngine3D
  Height = 20
  Placement = pos=(15.75,114,58.525) rot=(0,0.707107,0.707107;3.14159rad)
  Radius = 1.5
FEATURE [Part::Cylinder] Cylinder1673  label="Válec1673"
  Angle = 360
  AttacherType = Attacher::AttachEngine3D
  Height = 20
  Placement = pos=(15.75,114,39.475) rot=(0,0.707107,0.707107;3.14159rad)
  Radius = 1.5
FEATURE [Part::Compound] Compound822
  Links = -> [Cylinder1673,Cylinder1672]
  Placement = pos=(-49,0,-96) rot=(0.57735,0.57735,0.57735;2.0944rad)
FEATURE [Part::Compound] Compound823
  Links = -> [Compound822]
  Placement = pos=(0,74,-80) rot=(0,0,1;0rad)
FEATURE [Part::Cut] Cut333
  Base = -> Cut320
  Tool = -> Compound821
FEATURE [Part::Cut] Cut334
  Base = -> Cut327
  Tool = -> Compound823
FEATURE [Part::Compound] Compound825  label="J-max_encoder-inhold2"
  Links = -> [Chamfer043,Chamfer044,Cut321]
FEATURE [Part::Chamfer] Chamfer046
  Base = -> Cut333
  Edges = 2 edges r=4: [Edge3,Edge18]
FEATURE [Part::Cylinder] Cylinder1674  label="Válec1674"
  Angle = 360
  AttacherType = Attacher::AttachEngine3D
  Height = 4
  Placement = pos=(0,90,-53) rot=(0,0,1;0rad)
  Radius = 5
FEATURE [Part::FeaturePython] Tube064  # WARN: FeaturePython — macro-defined, semantics opaque (R4)
  AttacherType = Attacher::AttachEngine3D
  Height = 1
  InnerRadius = 4
  OuterRadius = 5
  Placement = pos=(0,90,-54) rot=(0,0,1;0rad)
FEATURE [Part::Compound] Compound826
  Links = -> [Cut334,Tube064]
FEATURE [Part::Chamfer] Chamfer047
  Base = -> Compound826
  Edges = 2 edges r=4: [Edge3,Edge18]
FEATURE [Part::Chamfer] Chamfer048
  Base = -> Chamfer047
  Edges = 1 edges r=2: [Edge23]
FEATURE [Mesh::Feature] Mesh  label="J-max_encoder-outhold (Meshed)"
FEATURE [Part::FeaturePython] Tube065  # WARN: FeaturePython — macro-defined, semantics opaque (R4)
  AttacherType = Attacher::AttachEngine3D
  Height = 1
  InnerRadius = 4
  OuterRadius = 5
  Placement = pos=(0,90,-34) rot=(0,0,1;0rad)
FEATURE [Part::Compound] Compound828  label="J-max_encoder-inhold"
  Links = -> [Tube065,Compound825]
FEATURE [Part::Compound] Compound829  label="J-max_encoder-sidehold"
  Links = -> [Cut323,Chamfer046]
FEATURE [Part::Cylinder] Cylinder1675  label="Válec1675"
  Angle = 360
  AttacherType = Attacher::AttachEngine3D
  Height = 20
  Placement = pos=(15.75,114,58.525) rot=(0,0.707107,0.707107;3.14159rad)
  Radius = 1.5
FEATURE [Part::Cylinder] Cylinder1676  label="Válec1676"
  Angle = 360
  AttacherType = Attacher::AttachEngine3D
  Height = 20
  Placement = pos=(15.75,114,39.475) rot=(0,0.707107,0.707107;3.14159rad)
  Radius = 1.5
FEATURE [Part::Compound] Compound830
  Links = -> [Cylinder1676,Cylinder1675]
  Placement = pos=(-49,0,-96) rot=(0.57735,0.57735,0.57735;2.0944rad)
FEATURE [Part::Compound] Compound831
  Links = -> [Compound830]
  Placement = pos=(0,74,-72) rot=(0,0,1;0rad)
FEATURE [Part::Cut] Cut335
  Base = -> Chamfer041
  Tool = -> Compound831
FEATURE [Part::Compound] Compound832  label="J-max_encoder-outhold"
  Links = -> [Chamfer048,Cut335]
FEATURE [Mesh::Feature] Mesh002  label="J-max_encoder-washer (Meshed)001"
FEATURE [Mesh::Feature] Mesh003  label="J-max_encoder-inhold (Meshed)"
FEATURE [Mesh::Feature] Mesh004  label="J-max_encoder-sidehold (Meshed)"
FEATURE [Mesh::Feature] Mesh005  label="J-max_encoder-outhold (Meshed)001"
